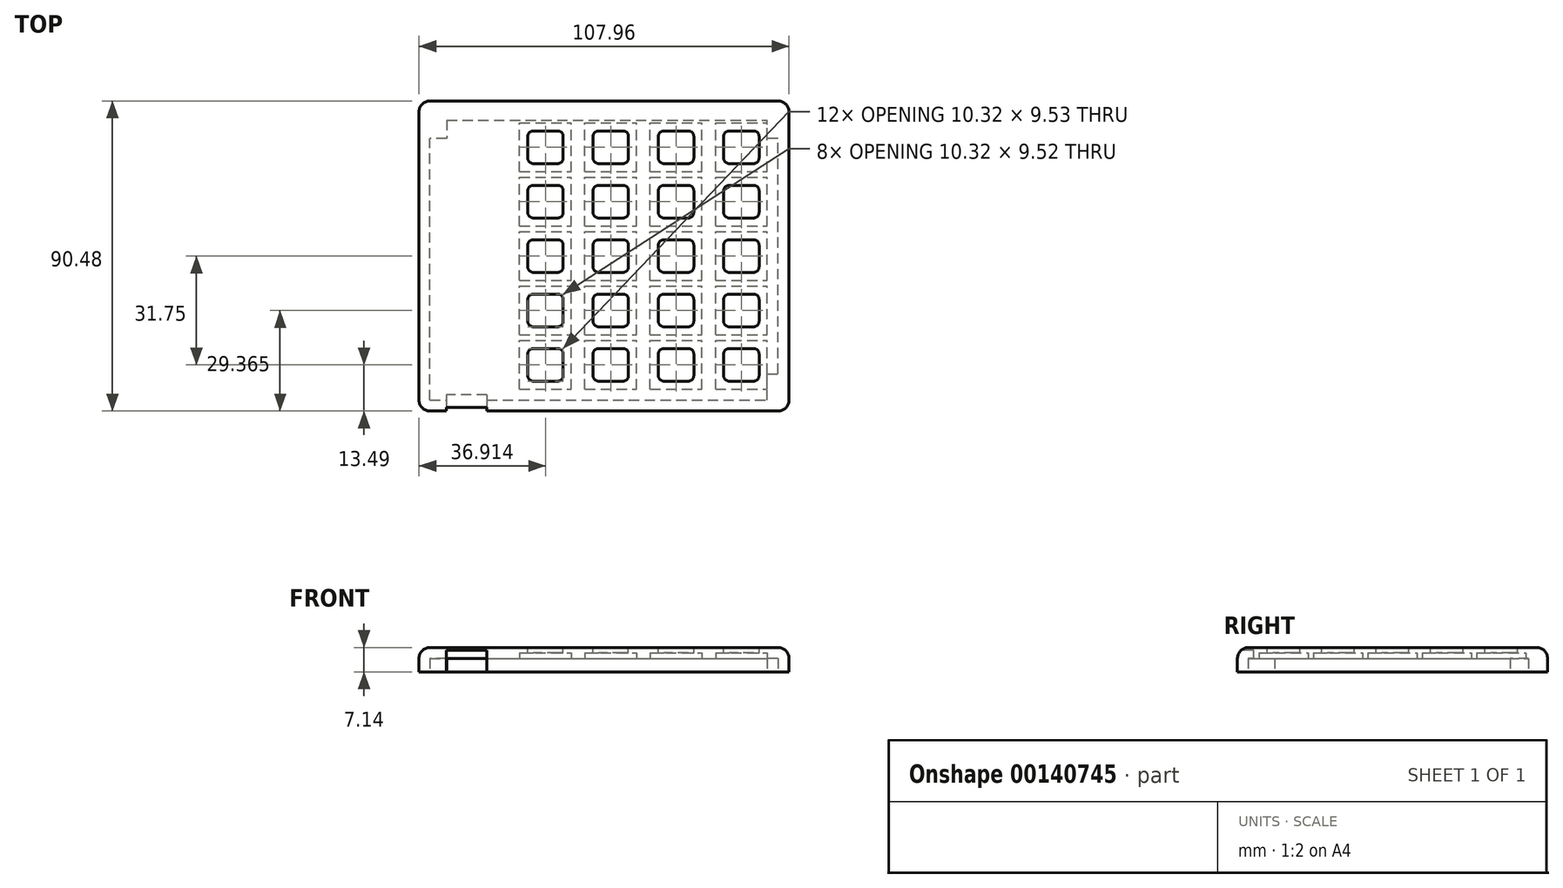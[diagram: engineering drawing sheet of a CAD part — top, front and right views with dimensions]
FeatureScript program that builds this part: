
annotation { "Feature Type Name" : "Feature", "Feature Type Description" : "" }
export const myFeature = defineFeature(function(context is Context, id is Id, definition is map)
    precondition{}
    {
        {
            var Q0;
            Q0=qCreatedBy(makeId("Top.planeOp"),FACE);
            var sketch = newSketch(context, id + "F0", { "sketchPlane" : qUnion([Q0])});
            skLineSegment(sketch, "E0.bottom", {"start": v(53.98, -45.24) * mm, "end": v(-53.98, -45.24) * mm});
            skLineSegment(sketch, "E0.top", {"start": v(53.98, 45.24) * mm, "end": v(-53.98, 45.24) * mm});
            skLineSegment(sketch, "E0.left", {"start": v(53.98, -45.24) * mm, "end": v(53.98, 45.24) * mm});
            skLineSegment(sketch, "E0.right", {"start": v(-53.98, -45.24) * mm, "end": v(-53.97, 45.24) * mm});
            skPoint(sketch, "E0.middle", {"position": v(0, 0) * mm});
            skSolve(sketch);
        }
        {
            var Q0;
            Q0=makeQuery(id+"F0.imprint","IMPRINT",FACE,{"disambiguationData":[TD([[makeQuery(id+"F0.imprint","IMPRINT",EDGE,{"derivedFrom":sQuery(id+"F0.wireOp",EDGE,"E0.bottom")}),-1.0]])]});
            extrude(context, id + "F1", {"entities" : qUnion([Q0]), "depth" : 7.14 * mm});
        }
        {
            var Q0;
            Q0=makeQuery(id+"F1.opExtrude","CAP_FACE",FACE,{"disambiguationData":[OSD([sQuery(id+"F0.wireOp",EDGE,"E0.bottom"),sQuery(id+"F0.wireOp",EDGE,"E0.top"),sQuery(id+"F0.wireOp",EDGE,"E0.left"),sQuery(id+"F0.wireOp",EDGE,"E0.right")])],"isStart":true});
            var sketch = newSketch(context, id + "F2", { "sketchPlane" : qUnion([Q0])});
            skLineSegment(sketch, "E1.0.0", {"start": v(53.98, 45.24) * mm, "end": v(-53.98, 45.24) * mm});
            skLineSegment(sketch, "E1.0.1", {"start": v(-53.98, 45.24) * mm, "end": v(-53.97, -45.24) * mm});
            skLineSegment(sketch, "E1.0.2", {"start": v(-53.97, -45.24) * mm, "end": v(53.98, -45.24) * mm});
            skLineSegment(sketch, "E1.0.3", {"start": v(53.98, -45.24) * mm, "end": v(53.98, 45.24) * mm});
            skLineSegment(sketch, "E2.bottom", {"start": v(-50.8, 42.07) * mm, "end": v(50.8, 42.07) * mm});
            skLineSegment(sketch, "E2.top", {"start": v(-50.8, -39.69) * mm, "end": v(50.8, -39.69) * mm});
            skLineSegment(sketch, "E2.left", {"start": v(-50.8, 42.07) * mm, "end": v(-50.8, -39.69) * mm});
            skLineSegment(sketch, "E2.right", {"start": v(50.8, 42.07) * mm, "end": v(50.8, -39.69) * mm});
            skSolve(sketch);
        }
        {
            var Q0;
            Q0=makeQuery(id+"F2.imprint","IMPRINT",FACE,{"disambiguationData":[TD([[makeQuery(id+"F2.imprint","IMPRINT",EDGE,{"derivedFrom":sQuery(id+"F2.wireOp",EDGE,"E2.bottom")}),-1.0]])]});
            extrude(context, id + "F3", {"entities" : qUnion([Q0]), "operationType" : NewBodyOperationType.REMOVE, "oppositeDirection" : true, "depth" : 3.97 * mm});
        }
        {
            var Q0;
            Q0=makeQuery(id+"F3.boolean.opBoolean","COPY",FACE,{"derivedFrom":makeQuery(id+"F3.opExtrude","CAP_FACE",FACE,{"disambiguationData":[OSD([sQuery(id+"F2.wireOp",EDGE,"E2.bottom"),sQuery(id+"F2.wireOp",EDGE,"E2.top"),sQuery(id+"F2.wireOp",EDGE,"E2.left"),sQuery(id+"F2.wireOp",EDGE,"E2.right")])],"isStart":false})});
            var sketch = newSketch(context, id + "F4", { "sketchPlane" : qUnion([Q0])});
            skLineSegment(sketch, "E3.0.0", {"start": v(50.8, 42.07) * mm, "end": v(-50.8, 42.07) * mm});
            skLineSegment(sketch, "E3.0.1", {"start": v(-50.8, 42.07) * mm, "end": v(-50.8, -39.69) * mm});
            skLineSegment(sketch, "E3.0.2", {"start": v(-50.8, -39.69) * mm, "end": v(50.8, -39.69) * mm});
            skLineSegment(sketch, "E3.0.3", {"start": v(50.8, -39.69) * mm, "end": v(50.8, 42.07) * mm});
            skLineSegment(sketch, "E4.bottom", {"start": v(50.8, 42.07) * mm, "end": v(50, 42.07) * mm});
            skLineSegment(sketch, "E4.top", {"start": v(50.8, 41.28) * mm, "end": v(50, 41.28) * mm});
            skLineSegment(sketch, "E4.left", {"start": v(50.8, 42.07) * mm, "end": v(50.8, 41.28) * mm});
            skLineSegment(sketch, "E4.right", {"start": v(50, 42.07) * mm, "end": v(50, 41.28) * mm});
            skLineSegment(sketch, "E5.bottom", {"start": v(50, 41.28) * mm, "end": v(46.04, 41.28) * mm});
            skLineSegment(sketch, "E5.top", {"start": v(50, 37.3) * mm, "end": v(46.04, 37.3) * mm});
            skLineSegment(sketch, "E5.left", {"start": v(50, 41.28) * mm, "end": v(50, 37.3) * mm});
            skLineSegment(sketch, "E5.right", {"start": v(46.04, 41.28) * mm, "end": v(46.04, 37.3) * mm});
            skLineSegment(sketch, "E6.bottom", {"start": v(46.04, 37.3) * mm, "end": v(34.13, 37.3) * mm});
            skLineSegment(sketch, "E6.top", {"start": v(46.04, 26.2) * mm, "end": v(34.13, 26.2) * mm});
            skLineSegment(sketch, "E6.left", {"start": v(46.04, 37.3) * mm, "end": v(46.04, 26.2) * mm});
            skLineSegment(sketch, "E6.right", {"start": v(34.13, 37.3) * mm, "end": v(34.13, 26.2) * mm});
            skLineSegment(sketch, "E7", {"start": v(41.14, -39.69) * mm, "end": v(41.14, -37.3) * mm});
            skLineSegment(sketch, "E8", {"start": v(-50.8, 34.78) * mm, "end": v(-23.02, 34.78) * mm});
            skLineSegment(sketch, "E9.0.1.0", {"start": v(46.04, 10.32) * mm, "end": v(34.13, 10.32) * mm});
            skLineSegment(sketch, "E9.0.1.1", {"start": v(46.04, 21.43) * mm, "end": v(46.04, 10.32) * mm});
            skLineSegment(sketch, "E9.0.1.2", {"start": v(46.04, 21.43) * mm, "end": v(34.13, 21.43) * mm});
            skLineSegment(sketch, "E9.0.1.3", {"start": v(34.13, 21.43) * mm, "end": v(34.13, 10.32) * mm});
            skLineSegment(sketch, "E9.0.2.0", {"start": v(46.04, -5.56) * mm, "end": v(34.13, -5.56) * mm});
            skLineSegment(sketch, "E9.0.2.1", {"start": v(46.04, 5.56) * mm, "end": v(46.04, -5.56) * mm});
            skLineSegment(sketch, "E9.0.2.2", {"start": v(46.04, 5.56) * mm, "end": v(34.13, 5.56) * mm});
            skLineSegment(sketch, "E9.0.2.3", {"start": v(34.13, 5.56) * mm, "end": v(34.13, -5.56) * mm});
            skLineSegment(sketch, "E9.0.3.0", {"start": v(46.04, -21.43) * mm, "end": v(34.13, -21.43) * mm});
            skLineSegment(sketch, "E9.0.3.1", {"start": v(46.04, -10.32) * mm, "end": v(46.04, -21.43) * mm});
            skLineSegment(sketch, "E9.0.3.2", {"start": v(46.04, -10.32) * mm, "end": v(34.13, -10.32) * mm});
            skLineSegment(sketch, "E9.0.3.3", {"start": v(34.13, -10.32) * mm, "end": v(34.13, -21.43) * mm});
            skLineSegment(sketch, "E9.0.4.0", {"start": v(46.04, -37.3) * mm, "end": v(34.13, -37.3) * mm});
            skLineSegment(sketch, "E9.0.4.1", {"start": v(46.04, -26.2) * mm, "end": v(46.04, -37.3) * mm});
            skLineSegment(sketch, "E9.0.4.2", {"start": v(46.04, -26.2) * mm, "end": v(34.13, -26.2) * mm});
            skLineSegment(sketch, "E9.0.4.3", {"start": v(34.13, -26.2) * mm, "end": v(34.13, -37.3) * mm});
            skLineSegment(sketch, "E9.1.0.0", {"start": v(26.99, 26.2) * mm, "end": v(15.08, 26.2) * mm});
            skLineSegment(sketch, "E9.1.0.1", {"start": v(26.99, 37.3) * mm, "end": v(26.99, 26.2) * mm});
            skLineSegment(sketch, "E9.1.0.2", {"start": v(26.99, 37.3) * mm, "end": v(15.08, 37.3) * mm});
            skLineSegment(sketch, "E9.1.0.3", {"start": v(15.08, 37.3) * mm, "end": v(15.08, 26.2) * mm});
            skLineSegment(sketch, "E9.1.1.0", {"start": v(26.99, 10.32) * mm, "end": v(15.08, 10.32) * mm});
            skLineSegment(sketch, "E9.1.1.1", {"start": v(26.99, 21.43) * mm, "end": v(26.99, 10.32) * mm});
            skLineSegment(sketch, "E9.1.1.2", {"start": v(26.99, 21.43) * mm, "end": v(15.08, 21.43) * mm});
            skLineSegment(sketch, "E9.1.1.3", {"start": v(15.08, 21.43) * mm, "end": v(15.08, 10.32) * mm});
            skLineSegment(sketch, "E9.1.2.0", {"start": v(26.99, -5.56) * mm, "end": v(15.08, -5.56) * mm});
            skLineSegment(sketch, "E9.1.2.1", {"start": v(26.99, 5.56) * mm, "end": v(26.99, -5.56) * mm});
            skLineSegment(sketch, "E9.1.2.2", {"start": v(26.99, 5.56) * mm, "end": v(15.08, 5.56) * mm});
            skLineSegment(sketch, "E9.1.2.3", {"start": v(15.08, 5.56) * mm, "end": v(15.08, -5.56) * mm});
            skLineSegment(sketch, "E9.1.3.0", {"start": v(26.99, -21.43) * mm, "end": v(15.08, -21.43) * mm});
            skLineSegment(sketch, "E9.1.3.1", {"start": v(26.99, -10.32) * mm, "end": v(26.99, -21.43) * mm});
            skLineSegment(sketch, "E9.1.3.2", {"start": v(26.99, -10.32) * mm, "end": v(15.08, -10.32) * mm});
            skLineSegment(sketch, "E9.1.3.3", {"start": v(15.08, -10.32) * mm, "end": v(15.08, -21.43) * mm});
            skLineSegment(sketch, "E9.1.4.0", {"start": v(26.99, -37.3) * mm, "end": v(15.08, -37.3) * mm});
            skLineSegment(sketch, "E9.1.4.1", {"start": v(26.99, -26.2) * mm, "end": v(26.99, -37.3) * mm});
            skLineSegment(sketch, "E9.1.4.2", {"start": v(26.99, -26.2) * mm, "end": v(15.08, -26.2) * mm});
            skLineSegment(sketch, "E9.1.4.3", {"start": v(15.08, -26.2) * mm, "end": v(15.08, -37.3) * mm});
            skLineSegment(sketch, "E9.2.0.0", {"start": v(7.94, 26.2) * mm, "end": v(-3.97, 26.2) * mm});
            skLineSegment(sketch, "E9.2.0.1", {"start": v(7.94, 37.3) * mm, "end": v(7.94, 26.2) * mm});
            skLineSegment(sketch, "E9.2.0.2", {"start": v(7.94, 37.3) * mm, "end": v(-3.97, 37.3) * mm});
            skLineSegment(sketch, "E9.2.0.3", {"start": v(-3.97, 37.3) * mm, "end": v(-3.97, 26.2) * mm});
            skLineSegment(sketch, "E9.2.1.0", {"start": v(7.94, 10.32) * mm, "end": v(-3.97, 10.32) * mm});
            skLineSegment(sketch, "E9.2.1.1", {"start": v(7.94, 21.43) * mm, "end": v(7.94, 10.32) * mm});
            skLineSegment(sketch, "E9.2.1.2", {"start": v(7.94, 21.43) * mm, "end": v(-3.97, 21.43) * mm});
            skLineSegment(sketch, "E9.2.1.3", {"start": v(-3.97, 21.43) * mm, "end": v(-3.97, 10.32) * mm});
            skLineSegment(sketch, "E9.2.2.0", {"start": v(7.94, -5.56) * mm, "end": v(-3.97, -5.56) * mm});
            skLineSegment(sketch, "E9.2.2.1", {"start": v(7.94, 5.56) * mm, "end": v(7.94, -5.56) * mm});
            skLineSegment(sketch, "E9.2.2.2", {"start": v(7.94, 5.56) * mm, "end": v(-3.97, 5.56) * mm});
            skLineSegment(sketch, "E9.2.2.3", {"start": v(-3.97, 5.56) * mm, "end": v(-3.97, -5.56) * mm});
            skLineSegment(sketch, "E9.2.3.0", {"start": v(7.94, -21.43) * mm, "end": v(-3.97, -21.43) * mm});
            skLineSegment(sketch, "E9.2.3.1", {"start": v(7.94, -10.32) * mm, "end": v(7.94, -21.43) * mm});
            skLineSegment(sketch, "E9.2.3.2", {"start": v(7.94, -10.32) * mm, "end": v(-3.97, -10.32) * mm});
            skLineSegment(sketch, "E9.2.3.3", {"start": v(-3.97, -10.32) * mm, "end": v(-3.97, -21.43) * mm});
            skLineSegment(sketch, "E9.2.4.0", {"start": v(7.94, -37.3) * mm, "end": v(-3.97, -37.3) * mm});
            skLineSegment(sketch, "E9.2.4.1", {"start": v(7.94, -26.2) * mm, "end": v(7.94, -37.3) * mm});
            skLineSegment(sketch, "E9.2.4.2", {"start": v(7.94, -26.2) * mm, "end": v(-3.97, -26.2) * mm});
            skLineSegment(sketch, "E9.2.4.3", {"start": v(-3.97, -26.2) * mm, "end": v(-3.97, -37.3) * mm});
            skLineSegment(sketch, "E9.3.0.0", {"start": v(-11.11, 26.2) * mm, "end": v(-23.02, 26.2) * mm});
            skLineSegment(sketch, "E9.3.0.1", {"start": v(-11.11, 37.3) * mm, "end": v(-11.11, 26.2) * mm});
            skLineSegment(sketch, "E9.3.0.2", {"start": v(-11.11, 37.3) * mm, "end": v(-23.02, 37.3) * mm});
            skLineSegment(sketch, "E9.3.0.3", {"start": v(-23.02, 37.3) * mm, "end": v(-23.02, 26.2) * mm});
            skLineSegment(sketch, "E9.3.1.0", {"start": v(-11.11, 10.32) * mm, "end": v(-23.02, 10.32) * mm});
            skLineSegment(sketch, "E9.3.1.1", {"start": v(-11.11, 21.43) * mm, "end": v(-11.11, 10.32) * mm});
            skLineSegment(sketch, "E9.3.1.2", {"start": v(-11.11, 21.43) * mm, "end": v(-23.02, 21.43) * mm});
            skLineSegment(sketch, "E9.3.1.3", {"start": v(-23.02, 21.43) * mm, "end": v(-23.02, 10.32) * mm});
            skLineSegment(sketch, "E9.3.2.0", {"start": v(-11.11, -5.56) * mm, "end": v(-23.02, -5.56) * mm});
            skLineSegment(sketch, "E9.3.2.1", {"start": v(-11.11, 5.56) * mm, "end": v(-11.11, -5.56) * mm});
            skLineSegment(sketch, "E9.3.2.2", {"start": v(-11.11, 5.56) * mm, "end": v(-23.02, 5.56) * mm});
            skLineSegment(sketch, "E9.3.2.3", {"start": v(-23.02, 5.56) * mm, "end": v(-23.02, -5.56) * mm});
            skLineSegment(sketch, "E9.3.3.0", {"start": v(-11.11, -21.43) * mm, "end": v(-23.02, -21.43) * mm});
            skLineSegment(sketch, "E9.3.3.1", {"start": v(-11.11, -10.32) * mm, "end": v(-11.11, -21.43) * mm});
            skLineSegment(sketch, "E9.3.3.2", {"start": v(-11.11, -10.32) * mm, "end": v(-23.02, -10.32) * mm});
            skLineSegment(sketch, "E9.3.3.3", {"start": v(-23.02, -10.32) * mm, "end": v(-23.02, -21.43) * mm});
            skLineSegment(sketch, "E9.3.4.0", {"start": v(-11.11, -37.3) * mm, "end": v(-23.02, -37.3) * mm});
            skLineSegment(sketch, "E9.3.4.1", {"start": v(-11.11, -26.2) * mm, "end": v(-11.11, -37.3) * mm});
            skLineSegment(sketch, "E9.3.4.2", {"start": v(-11.11, -26.2) * mm, "end": v(-23.02, -26.2) * mm});
            skLineSegment(sketch, "E9.3.4.3", {"start": v(-23.02, -26.2) * mm, "end": v(-23.02, -37.3) * mm});
            skLineSegment(sketch, "E9.direction1", {"start": v(34.13, 26.2) * mm, "end": v(15.08, 26.2) * mm, "construction": true});
            skLineSegment(sketch, "E9.direction2", {"start": v(34.13, 26.2) * mm, "end": v(34.13, 10.32) * mm, "construction": true});
            skLineSegment(sketch, "E10.bottom", {"start": v(32.54, 38.9) * mm, "end": v(47.62, 38.9) * mm});
            skLineSegment(sketch, "E10.top", {"start": v(32.54, 24.6) * mm, "end": v(47.62, 24.6) * mm});
            skLineSegment(sketch, "E10.left", {"start": v(32.54, 38.9) * mm, "end": v(32.54, 24.6) * mm});
            skLineSegment(sketch, "E10.right", {"start": v(47.62, 38.9) * mm, "end": v(47.62, 24.6) * mm});
            skLineSegment(sketch, "E11.0.1.0", {"start": v(32.54, 8.73) * mm, "end": v(47.62, 8.73) * mm});
            skLineSegment(sketch, "E11.0.1.1", {"start": v(32.54, 23.02) * mm, "end": v(32.54, 8.73) * mm});
            skLineSegment(sketch, "E11.0.1.2", {"start": v(32.54, 23.02) * mm, "end": v(47.62, 23.02) * mm});
            skLineSegment(sketch, "E11.0.1.3", {"start": v(47.62, 23.02) * mm, "end": v(47.62, 8.73) * mm});
            skLineSegment(sketch, "E11.0.2.0", {"start": v(32.54, -7.14) * mm, "end": v(47.62, -7.14) * mm});
            skLineSegment(sketch, "E11.0.2.1", {"start": v(32.54, 7.14) * mm, "end": v(32.54, -7.14) * mm});
            skLineSegment(sketch, "E11.0.2.2", {"start": v(32.54, 7.14) * mm, "end": v(47.62, 7.14) * mm});
            skLineSegment(sketch, "E11.0.2.3", {"start": v(47.62, 7.14) * mm, "end": v(47.62, -7.14) * mm});
            skLineSegment(sketch, "E11.0.3.0", {"start": v(32.54, -23.02) * mm, "end": v(47.62, -23.02) * mm});
            skLineSegment(sketch, "E11.0.3.1", {"start": v(32.54, -8.73) * mm, "end": v(32.54, -23.02) * mm});
            skLineSegment(sketch, "E11.0.3.2", {"start": v(32.54, -8.73) * mm, "end": v(47.62, -8.73) * mm});
            skLineSegment(sketch, "E11.0.3.3", {"start": v(47.62, -8.73) * mm, "end": v(47.62, -23.02) * mm});
            skLineSegment(sketch, "E11.0.4.0", {"start": v(32.54, -38.9) * mm, "end": v(47.62, -38.9) * mm});
            skLineSegment(sketch, "E11.0.4.1", {"start": v(32.54, -24.6) * mm, "end": v(32.54, -38.9) * mm});
            skLineSegment(sketch, "E11.0.4.2", {"start": v(32.54, -24.6) * mm, "end": v(47.62, -24.6) * mm});
            skLineSegment(sketch, "E11.0.4.3", {"start": v(47.62, -24.6) * mm, "end": v(47.62, -38.9) * mm});
            skLineSegment(sketch, "E11.1.0.0", {"start": v(13.5, 24.6) * mm, "end": v(28.57, 24.6) * mm});
            skLineSegment(sketch, "E11.1.0.1", {"start": v(13.5, 38.9) * mm, "end": v(13.5, 24.6) * mm});
            skLineSegment(sketch, "E11.1.0.2", {"start": v(13.5, 38.9) * mm, "end": v(28.57, 38.9) * mm});
            skLineSegment(sketch, "E11.1.0.3", {"start": v(28.57, 38.9) * mm, "end": v(28.57, 24.6) * mm});
            skLineSegment(sketch, "E11.1.1.0", {"start": v(13.5, 8.73) * mm, "end": v(28.57, 8.73) * mm});
            skLineSegment(sketch, "E11.1.1.1", {"start": v(13.5, 23.02) * mm, "end": v(13.5, 8.73) * mm});
            skLineSegment(sketch, "E11.1.1.2", {"start": v(13.5, 23.02) * mm, "end": v(28.57, 23.02) * mm});
            skLineSegment(sketch, "E11.1.1.3", {"start": v(28.57, 23.02) * mm, "end": v(28.57, 8.73) * mm});
            skLineSegment(sketch, "E11.1.2.0", {"start": v(13.5, -7.14) * mm, "end": v(28.57, -7.14) * mm});
            skLineSegment(sketch, "E11.1.2.1", {"start": v(13.5, 7.14) * mm, "end": v(13.5, -7.14) * mm});
            skLineSegment(sketch, "E11.1.2.2", {"start": v(13.5, 7.14) * mm, "end": v(28.57, 7.14) * mm});
            skLineSegment(sketch, "E11.1.2.3", {"start": v(28.57, 7.14) * mm, "end": v(28.57, -7.14) * mm});
            skLineSegment(sketch, "E11.1.3.0", {"start": v(13.5, -23.02) * mm, "end": v(28.57, -23.02) * mm});
            skLineSegment(sketch, "E11.1.3.1", {"start": v(13.5, -8.73) * mm, "end": v(13.5, -23.02) * mm});
            skLineSegment(sketch, "E11.1.3.2", {"start": v(13.5, -8.73) * mm, "end": v(28.57, -8.73) * mm});
            skLineSegment(sketch, "E11.1.3.3", {"start": v(28.57, -8.73) * mm, "end": v(28.57, -23.02) * mm});
            skLineSegment(sketch, "E11.1.4.0", {"start": v(13.5, -38.9) * mm, "end": v(28.57, -38.9) * mm});
            skLineSegment(sketch, "E11.1.4.1", {"start": v(13.5, -24.6) * mm, "end": v(13.5, -38.9) * mm});
            skLineSegment(sketch, "E11.1.4.2", {"start": v(13.5, -24.6) * mm, "end": v(28.57, -24.6) * mm});
            skLineSegment(sketch, "E11.1.4.3", {"start": v(28.57, -24.6) * mm, "end": v(28.57, -38.9) * mm});
            skLineSegment(sketch, "E11.2.0.0", {"start": v(-5.56, 24.6) * mm, "end": v(9.52, 24.6) * mm});
            skLineSegment(sketch, "E11.2.0.1", {"start": v(-5.56, 38.9) * mm, "end": v(-5.56, 24.6) * mm});
            skLineSegment(sketch, "E11.2.0.2", {"start": v(-5.56, 38.9) * mm, "end": v(9.52, 38.9) * mm});
            skLineSegment(sketch, "E11.2.0.3", {"start": v(9.52, 38.9) * mm, "end": v(9.52, 24.6) * mm});
            skLineSegment(sketch, "E11.2.1.0", {"start": v(-5.56, 8.73) * mm, "end": v(9.52, 8.73) * mm});
            skLineSegment(sketch, "E11.2.1.1", {"start": v(-5.56, 23.02) * mm, "end": v(-5.56, 8.73) * mm});
            skLineSegment(sketch, "E11.2.1.2", {"start": v(-5.56, 23.02) * mm, "end": v(9.52, 23.02) * mm});
            skLineSegment(sketch, "E11.2.1.3", {"start": v(9.52, 23.02) * mm, "end": v(9.52, 8.73) * mm});
            skLineSegment(sketch, "E11.2.2.0", {"start": v(-5.56, -7.14) * mm, "end": v(9.52, -7.14) * mm});
            skLineSegment(sketch, "E11.2.2.1", {"start": v(-5.56, 7.14) * mm, "end": v(-5.56, -7.14) * mm});
            skLineSegment(sketch, "E11.2.2.2", {"start": v(-5.56, 7.14) * mm, "end": v(9.52, 7.14) * mm});
            skLineSegment(sketch, "E11.2.2.3", {"start": v(9.52, 7.14) * mm, "end": v(9.52, -7.14) * mm});
            skLineSegment(sketch, "E11.2.3.0", {"start": v(-5.56, -23.02) * mm, "end": v(9.52, -23.02) * mm});
            skLineSegment(sketch, "E11.2.3.1", {"start": v(-5.56, -8.73) * mm, "end": v(-5.56, -23.02) * mm});
            skLineSegment(sketch, "E11.2.3.2", {"start": v(-5.56, -8.73) * mm, "end": v(9.52, -8.73) * mm});
            skLineSegment(sketch, "E11.2.3.3", {"start": v(9.52, -8.73) * mm, "end": v(9.52, -23.02) * mm});
            skLineSegment(sketch, "E11.2.4.0", {"start": v(-5.56, -38.9) * mm, "end": v(9.52, -38.9) * mm});
            skLineSegment(sketch, "E11.2.4.1", {"start": v(-5.56, -24.6) * mm, "end": v(-5.56, -38.9) * mm});
            skLineSegment(sketch, "E11.2.4.2", {"start": v(-5.56, -24.6) * mm, "end": v(9.52, -24.6) * mm});
            skLineSegment(sketch, "E11.2.4.3", {"start": v(9.52, -24.6) * mm, "end": v(9.52, -38.9) * mm});
            skLineSegment(sketch, "E11.3.0.0", {"start": v(-24.6, 24.6) * mm, "end": v(-9.53, 24.6) * mm});
            skLineSegment(sketch, "E11.3.0.1", {"start": v(-24.6, 38.9) * mm, "end": v(-24.6, 24.6) * mm});
            skLineSegment(sketch, "E11.3.0.2", {"start": v(-24.6, 38.9) * mm, "end": v(-9.53, 38.9) * mm});
            skLineSegment(sketch, "E11.3.0.3", {"start": v(-9.53, 38.9) * mm, "end": v(-9.53, 24.6) * mm});
            skLineSegment(sketch, "E11.3.1.0", {"start": v(-24.6, 8.73) * mm, "end": v(-9.53, 8.73) * mm});
            skLineSegment(sketch, "E11.3.1.1", {"start": v(-24.6, 23.02) * mm, "end": v(-24.6, 8.73) * mm});
            skLineSegment(sketch, "E11.3.1.2", {"start": v(-24.6, 23.02) * mm, "end": v(-9.53, 23.02) * mm});
            skLineSegment(sketch, "E11.3.1.3", {"start": v(-9.53, 23.02) * mm, "end": v(-9.53, 8.73) * mm});
            skLineSegment(sketch, "E11.3.2.0", {"start": v(-24.6, -7.14) * mm, "end": v(-9.53, -7.14) * mm});
            skLineSegment(sketch, "E11.3.2.1", {"start": v(-24.6, 7.14) * mm, "end": v(-24.6, -7.14) * mm});
            skLineSegment(sketch, "E11.3.2.2", {"start": v(-24.6, 7.14) * mm, "end": v(-9.53, 7.14) * mm});
            skLineSegment(sketch, "E11.3.2.3", {"start": v(-9.53, 7.14) * mm, "end": v(-9.53, -7.14) * mm});
            skLineSegment(sketch, "E11.3.3.0", {"start": v(-24.6, -23.02) * mm, "end": v(-9.53, -23.02) * mm});
            skLineSegment(sketch, "E11.3.3.1", {"start": v(-24.6, -8.73) * mm, "end": v(-24.6, -23.02) * mm});
            skLineSegment(sketch, "E11.3.3.2", {"start": v(-24.6, -8.73) * mm, "end": v(-9.53, -8.73) * mm});
            skLineSegment(sketch, "E11.3.3.3", {"start": v(-9.53, -8.73) * mm, "end": v(-9.53, -23.02) * mm});
            skLineSegment(sketch, "E11.3.4.0", {"start": v(-24.6, -38.9) * mm, "end": v(-9.53, -38.9) * mm});
            skLineSegment(sketch, "E11.3.4.1", {"start": v(-24.6, -24.6) * mm, "end": v(-24.6, -38.9) * mm});
            skLineSegment(sketch, "E11.3.4.2", {"start": v(-24.6, -24.6) * mm, "end": v(-9.53, -24.6) * mm});
            skLineSegment(sketch, "E11.3.4.3", {"start": v(-9.53, -24.6) * mm, "end": v(-9.53, -38.9) * mm});
            skLineSegment(sketch, "E11.direction1", {"start": v(32.54, 24.6) * mm, "end": v(13.5, 24.6) * mm, "construction": true});
            skLineSegment(sketch, "E11.direction2", {"start": v(32.54, 24.6) * mm, "end": v(32.54, 8.73) * mm, "construction": true});
            skSolve(sketch);
        }
        {
            var Q0;
            {var subQ3=sQuery(id+"F4.wireOp",EDGE,"E9.3.0.0");Q0=makeQuery(id+"F4.imprint","IMPRINT",FACE,{"disambiguationData":[TD([[makeQuery(id+"F4.imprint","IMPRINT",EDGE,{"derivedFrom":subQ3}),1.0]])]});}
            var Q1;
            {var subQ3=sQuery(id+"F4.wireOp",EDGE,"E9.3.0.0");Q1=makeQuery(id+"F4.imprint","IMPRINT",FACE,{"disambiguationData":[TD([[makeQuery(id+"F4.imprint","IMPRINT",EDGE,{"derivedFrom":subQ3}),-1.0]])]});}
            var Q2;
            Q2=makeQuery(id+"F4.imprint","IMPRINT",FACE,{"disambiguationData":[TD([[makeQuery(id+"F4.imprint","IMPRINT",EDGE,{"derivedFrom":sQuery(id+"F4.wireOp",EDGE,"E9.2.0.0")}),1.0]])]});
            var Q3;
            Q3=makeQuery(id+"F4.imprint","IMPRINT",FACE,{"disambiguationData":[TD([[makeQuery(id+"F4.imprint","IMPRINT",EDGE,{"derivedFrom":sQuery(id+"F4.wireOp",EDGE,"E9.2.0.0")}),-1.0]])]});
            var Q4;
            Q4=makeQuery(id+"F4.imprint","IMPRINT",FACE,{"disambiguationData":[TD([[makeQuery(id+"F4.imprint","IMPRINT",EDGE,{"derivedFrom":sQuery(id+"F4.wireOp",EDGE,"E9.1.0.0")}),1.0]])]});
            var Q5;
            Q5=makeQuery(id+"F4.imprint","IMPRINT",FACE,{"disambiguationData":[TD([[makeQuery(id+"F4.imprint","IMPRINT",EDGE,{"derivedFrom":sQuery(id+"F4.wireOp",EDGE,"E9.1.0.0")}),-1.0]])]});
            var Q6;
            {var subQ1=sQuery(id+"F4.wireOp",EDGE,"E6.bottom");Q6=makeQuery(id+"F4.imprint","IMPRINT",FACE,{"disambiguationData":[TD([[makeQuery(id+"F4.imprint","IMPRINT",EDGE,{"derivedFrom":subQ1}),-1.0]])]});}
            var Q7;
            Q7=makeQuery(id+"F4.imprint","IMPRINT",FACE,{"disambiguationData":[TD([[makeQuery(id+"F4.imprint","IMPRINT",EDGE,{"derivedFrom":sQuery(id+"F4.wireOp",EDGE,"E6.bottom")}),1.0]])]});
            var Q8;
            Q8=makeQuery(id+"F4.imprint","IMPRINT",FACE,{"disambiguationData":[TD([[makeQuery(id+"F4.imprint","IMPRINT",EDGE,{"derivedFrom":sQuery(id+"F4.wireOp",EDGE,"E9.0.1.0")}),1.0]])]});
            var Q9;
            Q9=makeQuery(id+"F4.imprint","IMPRINT",FACE,{"disambiguationData":[TD([[makeQuery(id+"F4.imprint","IMPRINT",EDGE,{"derivedFrom":sQuery(id+"F4.wireOp",EDGE,"E9.0.1.0")}),-1.0]])]});
            var Q10;
            Q10=makeQuery(id+"F4.imprint","IMPRINT",FACE,{"disambiguationData":[TD([[makeQuery(id+"F4.imprint","IMPRINT",EDGE,{"derivedFrom":sQuery(id+"F4.wireOp",EDGE,"E9.1.1.0")}),1.0]])]});
            var Q11;
            Q11=makeQuery(id+"F4.imprint","IMPRINT",FACE,{"disambiguationData":[TD([[makeQuery(id+"F4.imprint","IMPRINT",EDGE,{"derivedFrom":sQuery(id+"F4.wireOp",EDGE,"E9.1.1.0")}),-1.0]])]});
            var Q12;
            Q12=makeQuery(id+"F4.imprint","IMPRINT",FACE,{"disambiguationData":[TD([[makeQuery(id+"F4.imprint","IMPRINT",EDGE,{"derivedFrom":sQuery(id+"F4.wireOp",EDGE,"E9.2.1.0")}),1.0]])]});
            var Q13;
            Q13=makeQuery(id+"F4.imprint","IMPRINT",FACE,{"disambiguationData":[TD([[makeQuery(id+"F4.imprint","IMPRINT",EDGE,{"derivedFrom":sQuery(id+"F4.wireOp",EDGE,"E9.2.1.0")}),-1.0]])]});
            var Q14;
            Q14=makeQuery(id+"F4.imprint","IMPRINT",FACE,{"disambiguationData":[TD([[makeQuery(id+"F4.imprint","IMPRINT",EDGE,{"derivedFrom":sQuery(id+"F4.wireOp",EDGE,"E9.3.1.0")}),1.0]])]});
            var Q15;
            Q15=makeQuery(id+"F4.imprint","IMPRINT",FACE,{"disambiguationData":[TD([[makeQuery(id+"F4.imprint","IMPRINT",EDGE,{"derivedFrom":sQuery(id+"F4.wireOp",EDGE,"E9.3.1.0")}),-1.0]])]});
            var Q16;
            Q16=makeQuery(id+"F4.imprint","IMPRINT",FACE,{"disambiguationData":[TD([[makeQuery(id+"F4.imprint","IMPRINT",EDGE,{"derivedFrom":sQuery(id+"F4.wireOp",EDGE,"E9.3.2.0")}),1.0]])]});
            var Q17;
            Q17=makeQuery(id+"F4.imprint","IMPRINT",FACE,{"disambiguationData":[TD([[makeQuery(id+"F4.imprint","IMPRINT",EDGE,{"derivedFrom":sQuery(id+"F4.wireOp",EDGE,"E9.3.2.0")}),-1.0]])]});
            var Q18;
            Q18=makeQuery(id+"F4.imprint","IMPRINT",FACE,{"disambiguationData":[TD([[makeQuery(id+"F4.imprint","IMPRINT",EDGE,{"derivedFrom":sQuery(id+"F4.wireOp",EDGE,"E9.2.2.0")}),1.0]])]});
            var Q19;
            Q19=makeQuery(id+"F4.imprint","IMPRINT",FACE,{"disambiguationData":[TD([[makeQuery(id+"F4.imprint","IMPRINT",EDGE,{"derivedFrom":sQuery(id+"F4.wireOp",EDGE,"E9.2.2.0")}),-1.0]])]});
            var Q20;
            Q20=makeQuery(id+"F4.imprint","IMPRINT",FACE,{"disambiguationData":[TD([[makeQuery(id+"F4.imprint","IMPRINT",EDGE,{"derivedFrom":sQuery(id+"F4.wireOp",EDGE,"E9.1.2.0")}),1.0]])]});
            var Q21;
            Q21=makeQuery(id+"F4.imprint","IMPRINT",FACE,{"disambiguationData":[TD([[makeQuery(id+"F4.imprint","IMPRINT",EDGE,{"derivedFrom":sQuery(id+"F4.wireOp",EDGE,"E9.1.2.0")}),-1.0]])]});
            var Q22;
            Q22=makeQuery(id+"F4.imprint","IMPRINT",FACE,{"disambiguationData":[TD([[makeQuery(id+"F4.imprint","IMPRINT",EDGE,{"derivedFrom":sQuery(id+"F4.wireOp",EDGE,"E9.0.2.0")}),-1.0]])]});
            var Q23;
            Q23=makeQuery(id+"F4.imprint","IMPRINT",FACE,{"disambiguationData":[TD([[makeQuery(id+"F4.imprint","IMPRINT",EDGE,{"derivedFrom":sQuery(id+"F4.wireOp",EDGE,"E9.0.2.0")}),1.0]])]});
            var Q24;
            Q24=makeQuery(id+"F4.imprint","IMPRINT",FACE,{"disambiguationData":[TD([[makeQuery(id+"F4.imprint","IMPRINT",EDGE,{"derivedFrom":sQuery(id+"F4.wireOp",EDGE,"E9.3.3.0")}),1.0]])]});
            var Q25;
            Q25=makeQuery(id+"F4.imprint","IMPRINT",FACE,{"disambiguationData":[TD([[makeQuery(id+"F4.imprint","IMPRINT",EDGE,{"derivedFrom":sQuery(id+"F4.wireOp",EDGE,"E9.3.3.0")}),-1.0]])]});
            var Q26;
            Q26=makeQuery(id+"F4.imprint","IMPRINT",FACE,{"disambiguationData":[TD([[makeQuery(id+"F4.imprint","IMPRINT",EDGE,{"derivedFrom":sQuery(id+"F4.wireOp",EDGE,"E9.2.3.0")}),1.0]])]});
            var Q27;
            Q27=makeQuery(id+"F4.imprint","IMPRINT",FACE,{"disambiguationData":[TD([[makeQuery(id+"F4.imprint","IMPRINT",EDGE,{"derivedFrom":sQuery(id+"F4.wireOp",EDGE,"E9.2.3.0")}),-1.0]])]});
            var Q28;
            Q28=makeQuery(id+"F4.imprint","IMPRINT",FACE,{"disambiguationData":[TD([[makeQuery(id+"F4.imprint","IMPRINT",EDGE,{"derivedFrom":sQuery(id+"F4.wireOp",EDGE,"E9.1.3.0")}),1.0]])]});
            var Q29;
            Q29=makeQuery(id+"F4.imprint","IMPRINT",FACE,{"disambiguationData":[TD([[makeQuery(id+"F4.imprint","IMPRINT",EDGE,{"derivedFrom":sQuery(id+"F4.wireOp",EDGE,"E9.1.3.0")}),-1.0]])]});
            var Q30;
            Q30=makeQuery(id+"F4.imprint","IMPRINT",FACE,{"disambiguationData":[TD([[makeQuery(id+"F4.imprint","IMPRINT",EDGE,{"derivedFrom":sQuery(id+"F4.wireOp",EDGE,"E9.0.3.0")}),1.0]])]});
            var Q31;
            Q31=makeQuery(id+"F4.imprint","IMPRINT",FACE,{"disambiguationData":[TD([[makeQuery(id+"F4.imprint","IMPRINT",EDGE,{"derivedFrom":sQuery(id+"F4.wireOp",EDGE,"E9.0.3.0")}),-1.0]])]});
            var Q32;
            {var subQ3=sQuery(id+"F4.wireOp",EDGE,"E9.0.4.1");Q32=makeQuery(id+"F4.imprint","IMPRINT",FACE,{"disambiguationData":[TD([[makeQuery(id+"F4.imprint","IMPRINT",EDGE,{"derivedFrom":subQ3}),1.0]])]});}
            var Q33;
            {var subQ0=sQuery(id+"F4.wireOp",EDGE,"E9.0.4.1");Q33=makeQuery(id+"F4.imprint","IMPRINT",FACE,{"disambiguationData":[TD([[makeQuery(id+"F4.imprint","IMPRINT",EDGE,{"derivedFrom":subQ0}),-1.0]])]});}
            var Q34;
            Q34=makeQuery(id+"F4.imprint","IMPRINT",FACE,{"disambiguationData":[TD([[makeQuery(id+"F4.imprint","IMPRINT",EDGE,{"derivedFrom":sQuery(id+"F4.wireOp",EDGE,"E9.1.4.0")}),1.0]])]});
            var Q35;
            Q35=makeQuery(id+"F4.imprint","IMPRINT",FACE,{"disambiguationData":[TD([[makeQuery(id+"F4.imprint","IMPRINT",EDGE,{"derivedFrom":sQuery(id+"F4.wireOp",EDGE,"E9.1.4.0")}),-1.0]])]});
            var Q36;
            Q36=makeQuery(id+"F4.imprint","IMPRINT",FACE,{"disambiguationData":[TD([[makeQuery(id+"F4.imprint","IMPRINT",EDGE,{"derivedFrom":sQuery(id+"F4.wireOp",EDGE,"E9.2.4.0")}),1.0]])]});
            var Q37;
            Q37=makeQuery(id+"F4.imprint","IMPRINT",FACE,{"disambiguationData":[TD([[makeQuery(id+"F4.imprint","IMPRINT",EDGE,{"derivedFrom":sQuery(id+"F4.wireOp",EDGE,"E9.2.4.0")}),-1.0]])]});
            var Q38;
            Q38=makeQuery(id+"F4.imprint","IMPRINT",FACE,{"disambiguationData":[TD([[makeQuery(id+"F4.imprint","IMPRINT",EDGE,{"derivedFrom":sQuery(id+"F4.wireOp",EDGE,"E9.3.4.0")}),-1.0]])]});
            var Q39;
            Q39=makeQuery(id+"F4.imprint","IMPRINT",FACE,{"disambiguationData":[TD([[makeQuery(id+"F4.imprint","IMPRINT",EDGE,{"derivedFrom":sQuery(id+"F4.wireOp",EDGE,"E9.3.4.0")}),1.0]])]});
            var Q40;
            {var subQ3=sQuery(id+"F4.wireOp",EDGE,"E10.right");var subQ5=sQuery(id+"F4.wireOp",EDGE,"E10.bottom");var subQ7=makeQuery(id+"F4.imprint","INTERSECT",VERTEX,{"derivedFrom":[subQ5,subQ3]});Q40=makeQuery(id+"F4.imprint","IMPRINT",FACE,{"disambiguationData":[TD([[makeQuery(id+"F4.imprint","IMPRINT",EDGE,{"disambiguationData":[TD([[subQ7,1.0]])],"derivedFrom":subQ5}),-1.0]])]});}
            extrude(context, id + "F5", {"entities" : qUnion([Q0, Q1, Q2, Q3, Q4, Q5, Q6, Q7, Q8, Q9, Q10, Q11, Q12, Q13, Q14, Q15, Q16, Q17, Q18, Q19, Q20, Q21, Q22, Q23, Q24, Q25, Q26, Q27, Q28, Q29, Q30, Q31, Q32, Q33, Q34, Q35, Q36, Q37, Q38, Q39, Q40]), "operationType" : NewBodyOperationType.REMOVE, "oppositeDirection" : true, "depth" : 1.59 * mm});
        }
        {
            var Q0;
            Q0=makeQuery(id+"F5.boolean.opBoolean","COPY",FACE,{"derivedFrom":makeQuery(id+"F5.opExtrude","CAP_FACE",FACE,{"disambiguationData":[OSD([sQuery(id+"F4.wireOp",EDGE,"E11.1.0.0"),sQuery(id+"F4.wireOp",EDGE,"E11.1.0.1"),sQuery(id+"F4.wireOp",EDGE,"E11.1.0.2"),sQuery(id+"F4.wireOp",EDGE,"E11.1.0.3")])],"isStart":false})});
            var sketch = newSketch(context, id + "F6", { "sketchPlane" : qUnion([Q0])});
            skLineSegment(sketch, "E12.bottom", {"start": v(36.51, 36.51) * mm, "end": v(43.66, 36.51) * mm});
            skLineSegment(sketch, "E12.top", {"start": v(36.51, 26.99) * mm, "end": v(43.66, 26.99) * mm});
            skLineSegment(sketch, "E12.left", {"start": v(34.93, 34.93) * mm, "end": v(34.93, 28.58) * mm});
            skLineSegment(sketch, "E12.right", {"start": v(45.24, 34.93) * mm, "end": v(45.24, 28.58) * mm});
            skPoint(sketch, "E13.visualSharp", {"position": v(34.93, 36.51) * mm});
            skArc(sketch, "E13.filletArc", {"start": v(36.51, 36.51) * mm, "mid": v(35.39, 36.05) * mm, "end": v(34.93, 34.93) * mm});
            skPoint(sketch, "E14.visualSharp", {"position": v(45.24, 36.51) * mm});
            skArc(sketch, "E14.filletArc", {"start": v(45.24, 34.93) * mm, "mid": v(44.78, 36.05) * mm, "end": v(43.66, 36.51) * mm});
            skPoint(sketch, "E15.visualSharp", {"position": v(45.24, 26.99) * mm});
            skArc(sketch, "E15.filletArc", {"start": v(43.66, 26.99) * mm, "mid": v(44.78, 27.45) * mm, "end": v(45.24, 28.58) * mm});
            skPoint(sketch, "E16.visualSharp", {"position": v(34.93, 26.99) * mm});
            skArc(sketch, "E16.filletArc", {"start": v(34.93, 28.58) * mm, "mid": v(35.39, 27.45) * mm, "end": v(36.51, 26.99) * mm});
            skLineSegment(sketch, "E17.0.1.0", {"start": v(36.51, 11.11) * mm, "end": v(43.66, 11.11) * mm});
            skArc(sketch, "E17.0.1.1", {"start": v(34.93, 12.7) * mm, "mid": v(35.39, 11.58) * mm, "end": v(36.51, 11.11) * mm});
            skLineSegment(sketch, "E17.0.1.2", {"start": v(34.93, 19.05) * mm, "end": v(34.93, 12.7) * mm});
            skArc(sketch, "E17.0.1.3", {"start": v(36.51, 20.64) * mm, "mid": v(35.39, 20.17) * mm, "end": v(34.93, 19.05) * mm});
            skLineSegment(sketch, "E17.0.1.4", {"start": v(36.51, 20.64) * mm, "end": v(43.66, 20.64) * mm});
            skArc(sketch, "E17.0.1.5", {"start": v(45.24, 19.05) * mm, "mid": v(44.78, 20.17) * mm, "end": v(43.66, 20.64) * mm});
            skLineSegment(sketch, "E17.0.1.6", {"start": v(45.24, 19.05) * mm, "end": v(45.24, 12.7) * mm});
            skArc(sketch, "E17.0.1.7", {"start": v(43.66, 11.11) * mm, "mid": v(44.78, 11.58) * mm, "end": v(45.24, 12.7) * mm});
            skLineSegment(sketch, "E17.0.2.0", {"start": v(36.51, -4.76) * mm, "end": v(43.66, -4.76) * mm});
            skArc(sketch, "E17.0.2.1", {"start": v(34.93, -3.17) * mm, "mid": v(35.39, -4.3) * mm, "end": v(36.51, -4.76) * mm});
            skLineSegment(sketch, "E17.0.2.2", {"start": v(34.93, 3.18) * mm, "end": v(34.93, -3.17) * mm});
            skArc(sketch, "E17.0.2.3", {"start": v(36.51, 4.76) * mm, "mid": v(35.39, 4.3) * mm, "end": v(34.93, 3.18) * mm});
            skLineSegment(sketch, "E17.0.2.4", {"start": v(36.51, 4.76) * mm, "end": v(43.66, 4.76) * mm});
            skArc(sketch, "E17.0.2.5", {"start": v(45.24, 3.18) * mm, "mid": v(44.78, 4.3) * mm, "end": v(43.66, 4.76) * mm});
            skLineSegment(sketch, "E17.0.2.6", {"start": v(45.24, 3.18) * mm, "end": v(45.24, -3.17) * mm});
            skArc(sketch, "E17.0.2.7", {"start": v(43.66, -4.76) * mm, "mid": v(44.78, -4.3) * mm, "end": v(45.24, -3.17) * mm});
            skLineSegment(sketch, "E17.0.3.0", {"start": v(36.51, -20.64) * mm, "end": v(43.66, -20.64) * mm});
            skArc(sketch, "E17.0.3.1", {"start": v(34.93, -19.05) * mm, "mid": v(35.39, -20.17) * mm, "end": v(36.51, -20.64) * mm});
            skLineSegment(sketch, "E17.0.3.2", {"start": v(34.93, -12.7) * mm, "end": v(34.93, -19.05) * mm});
            skArc(sketch, "E17.0.3.3", {"start": v(36.51, -11.11) * mm, "mid": v(35.39, -11.58) * mm, "end": v(34.93, -12.7) * mm});
            skLineSegment(sketch, "E17.0.3.4", {"start": v(36.51, -11.11) * mm, "end": v(43.66, -11.11) * mm});
            skArc(sketch, "E17.0.3.5", {"start": v(45.24, -12.7) * mm, "mid": v(44.78, -11.58) * mm, "end": v(43.66, -11.11) * mm});
            skLineSegment(sketch, "E17.0.3.6", {"start": v(45.24, -12.7) * mm, "end": v(45.24, -19.05) * mm});
            skArc(sketch, "E17.0.3.7", {"start": v(43.66, -20.64) * mm, "mid": v(44.78, -20.17) * mm, "end": v(45.24, -19.05) * mm});
            skLineSegment(sketch, "E17.0.4.0", {"start": v(36.51, -36.51) * mm, "end": v(43.66, -36.51) * mm});
            skArc(sketch, "E17.0.4.1", {"start": v(34.93, -34.92) * mm, "mid": v(35.39, -36.05) * mm, "end": v(36.51, -36.51) * mm});
            skLineSegment(sketch, "E17.0.4.2", {"start": v(34.93, -28.57) * mm, "end": v(34.93, -34.92) * mm});
            skArc(sketch, "E17.0.4.3", {"start": v(36.51, -26.99) * mm, "mid": v(35.39, -27.45) * mm, "end": v(34.93, -28.57) * mm});
            skLineSegment(sketch, "E17.0.4.4", {"start": v(36.51, -26.99) * mm, "end": v(43.66, -26.99) * mm});
            skArc(sketch, "E17.0.4.5", {"start": v(45.24, -28.57) * mm, "mid": v(44.78, -27.45) * mm, "end": v(43.66, -26.99) * mm});
            skLineSegment(sketch, "E17.0.4.6", {"start": v(45.24, -28.57) * mm, "end": v(45.24, -34.92) * mm});
            skArc(sketch, "E17.0.4.7", {"start": v(43.66, -36.51) * mm, "mid": v(44.78, -36.05) * mm, "end": v(45.24, -34.92) * mm});
            skLineSegment(sketch, "E17.1.0.0", {"start": v(17.46, 26.99) * mm, "end": v(24.6, 26.99) * mm});
            skArc(sketch, "E17.1.0.1", {"start": v(15.88, 28.58) * mm, "mid": v(16.34, 27.45) * mm, "end": v(17.46, 26.99) * mm});
            skLineSegment(sketch, "E17.1.0.2", {"start": v(15.88, 34.93) * mm, "end": v(15.88, 28.58) * mm});
            skArc(sketch, "E17.1.0.3", {"start": v(17.46, 36.51) * mm, "mid": v(16.34, 36.05) * mm, "end": v(15.88, 34.93) * mm});
            skLineSegment(sketch, "E17.1.0.4", {"start": v(17.46, 36.51) * mm, "end": v(24.6, 36.51) * mm});
            skArc(sketch, "E17.1.0.5", {"start": v(26.2, 34.93) * mm, "mid": v(25.73, 36.05) * mm, "end": v(24.6, 36.51) * mm});
            skLineSegment(sketch, "E17.1.0.6", {"start": v(26.2, 34.93) * mm, "end": v(26.2, 28.58) * mm});
            skArc(sketch, "E17.1.0.7", {"start": v(24.6, 26.99) * mm, "mid": v(25.73, 27.45) * mm, "end": v(26.2, 28.58) * mm});
            skLineSegment(sketch, "E17.1.1.0", {"start": v(17.46, 11.11) * mm, "end": v(24.6, 11.11) * mm});
            skArc(sketch, "E17.1.1.1", {"start": v(15.88, 12.7) * mm, "mid": v(16.34, 11.58) * mm, "end": v(17.46, 11.11) * mm});
            skLineSegment(sketch, "E17.1.1.2", {"start": v(15.88, 19.05) * mm, "end": v(15.88, 12.7) * mm});
            skArc(sketch, "E17.1.1.3", {"start": v(17.46, 20.64) * mm, "mid": v(16.34, 20.17) * mm, "end": v(15.88, 19.05) * mm});
            skLineSegment(sketch, "E17.1.1.4", {"start": v(17.46, 20.64) * mm, "end": v(24.6, 20.64) * mm});
            skArc(sketch, "E17.1.1.5", {"start": v(26.2, 19.05) * mm, "mid": v(25.73, 20.17) * mm, "end": v(24.6, 20.64) * mm});
            skLineSegment(sketch, "E17.1.1.6", {"start": v(26.2, 19.05) * mm, "end": v(26.2, 12.7) * mm});
            skArc(sketch, "E17.1.1.7", {"start": v(24.6, 11.11) * mm, "mid": v(25.73, 11.58) * mm, "end": v(26.2, 12.7) * mm});
            skLineSegment(sketch, "E17.1.2.0", {"start": v(17.46, -4.76) * mm, "end": v(24.6, -4.76) * mm});
            skArc(sketch, "E17.1.2.1", {"start": v(15.88, -3.17) * mm, "mid": v(16.34, -4.3) * mm, "end": v(17.46, -4.76) * mm});
            skLineSegment(sketch, "E17.1.2.2", {"start": v(15.88, 3.18) * mm, "end": v(15.88, -3.17) * mm});
            skArc(sketch, "E17.1.2.3", {"start": v(17.46, 4.76) * mm, "mid": v(16.34, 4.3) * mm, "end": v(15.88, 3.18) * mm});
            skLineSegment(sketch, "E17.1.2.4", {"start": v(17.46, 4.76) * mm, "end": v(24.6, 4.76) * mm});
            skArc(sketch, "E17.1.2.5", {"start": v(26.2, 3.18) * mm, "mid": v(25.73, 4.3) * mm, "end": v(24.6, 4.76) * mm});
            skLineSegment(sketch, "E17.1.2.6", {"start": v(26.2, 3.18) * mm, "end": v(26.2, -3.17) * mm});
            skArc(sketch, "E17.1.2.7", {"start": v(24.6, -4.76) * mm, "mid": v(25.73, -4.3) * mm, "end": v(26.2, -3.17) * mm});
            skLineSegment(sketch, "E17.1.3.0", {"start": v(17.46, -20.64) * mm, "end": v(24.6, -20.64) * mm});
            skArc(sketch, "E17.1.3.1", {"start": v(15.88, -19.05) * mm, "mid": v(16.34, -20.17) * mm, "end": v(17.46, -20.64) * mm});
            skLineSegment(sketch, "E17.1.3.2", {"start": v(15.88, -12.7) * mm, "end": v(15.88, -19.05) * mm});
            skArc(sketch, "E17.1.3.3", {"start": v(17.46, -11.11) * mm, "mid": v(16.34, -11.58) * mm, "end": v(15.88, -12.7) * mm});
            skLineSegment(sketch, "E17.1.3.4", {"start": v(17.46, -11.11) * mm, "end": v(24.6, -11.11) * mm});
            skArc(sketch, "E17.1.3.5", {"start": v(26.2, -12.7) * mm, "mid": v(25.73, -11.58) * mm, "end": v(24.6, -11.11) * mm});
            skLineSegment(sketch, "E17.1.3.6", {"start": v(26.2, -12.7) * mm, "end": v(26.2, -19.05) * mm});
            skArc(sketch, "E17.1.3.7", {"start": v(24.6, -20.64) * mm, "mid": v(25.73, -20.17) * mm, "end": v(26.2, -19.05) * mm});
            skLineSegment(sketch, "E17.1.4.0", {"start": v(17.46, -36.51) * mm, "end": v(24.6, -36.51) * mm});
            skArc(sketch, "E17.1.4.1", {"start": v(15.88, -34.92) * mm, "mid": v(16.34, -36.05) * mm, "end": v(17.46, -36.51) * mm});
            skLineSegment(sketch, "E17.1.4.2", {"start": v(15.88, -28.57) * mm, "end": v(15.88, -34.92) * mm});
            skArc(sketch, "E17.1.4.3", {"start": v(17.46, -26.99) * mm, "mid": v(16.34, -27.45) * mm, "end": v(15.88, -28.57) * mm});
            skLineSegment(sketch, "E17.1.4.4", {"start": v(17.46, -26.99) * mm, "end": v(24.6, -26.99) * mm});
            skArc(sketch, "E17.1.4.5", {"start": v(26.2, -28.57) * mm, "mid": v(25.73, -27.45) * mm, "end": v(24.6, -26.99) * mm});
            skLineSegment(sketch, "E17.1.4.6", {"start": v(26.2, -28.57) * mm, "end": v(26.2, -34.92) * mm});
            skArc(sketch, "E17.1.4.7", {"start": v(24.6, -36.51) * mm, "mid": v(25.73, -36.05) * mm, "end": v(26.2, -34.92) * mm});
            skLineSegment(sketch, "E17.2.0.0", {"start": v(-1.59, 26.99) * mm, "end": v(5.56, 26.99) * mm});
            skArc(sketch, "E17.2.0.1", {"start": v(-3.17, 28.58) * mm, "mid": v(-2.71, 27.45) * mm, "end": v(-1.59, 26.99) * mm});
            skLineSegment(sketch, "E17.2.0.2", {"start": v(-3.17, 34.93) * mm, "end": v(-3.17, 28.58) * mm});
            skArc(sketch, "E17.2.0.3", {"start": v(-1.59, 36.51) * mm, "mid": v(-2.71, 36.05) * mm, "end": v(-3.17, 34.93) * mm});
            skLineSegment(sketch, "E17.2.0.4", {"start": v(-1.59, 36.51) * mm, "end": v(5.56, 36.51) * mm});
            skArc(sketch, "E17.2.0.5", {"start": v(7.14, 34.93) * mm, "mid": v(6.68, 36.05) * mm, "end": v(5.56, 36.51) * mm});
            skLineSegment(sketch, "E17.2.0.6", {"start": v(7.14, 34.93) * mm, "end": v(7.14, 28.58) * mm});
            skArc(sketch, "E17.2.0.7", {"start": v(5.56, 26.99) * mm, "mid": v(6.68, 27.45) * mm, "end": v(7.14, 28.58) * mm});
            skLineSegment(sketch, "E17.2.1.0", {"start": v(-1.59, 11.11) * mm, "end": v(5.56, 11.11) * mm});
            skArc(sketch, "E17.2.1.1", {"start": v(-3.17, 12.7) * mm, "mid": v(-2.71, 11.58) * mm, "end": v(-1.59, 11.11) * mm});
            skLineSegment(sketch, "E17.2.1.2", {"start": v(-3.17, 19.05) * mm, "end": v(-3.17, 12.7) * mm});
            skArc(sketch, "E17.2.1.3", {"start": v(-1.59, 20.64) * mm, "mid": v(-2.71, 20.17) * mm, "end": v(-3.17, 19.05) * mm});
            skLineSegment(sketch, "E17.2.1.4", {"start": v(-1.59, 20.64) * mm, "end": v(5.56, 20.64) * mm});
            skArc(sketch, "E17.2.1.5", {"start": v(7.14, 19.05) * mm, "mid": v(6.68, 20.17) * mm, "end": v(5.56, 20.64) * mm});
            skLineSegment(sketch, "E17.2.1.6", {"start": v(7.14, 19.05) * mm, "end": v(7.14, 12.7) * mm});
            skArc(sketch, "E17.2.1.7", {"start": v(5.56, 11.11) * mm, "mid": v(6.68, 11.58) * mm, "end": v(7.14, 12.7) * mm});
            skLineSegment(sketch, "E17.2.2.0", {"start": v(-1.59, -4.76) * mm, "end": v(5.56, -4.76) * mm});
            skArc(sketch, "E17.2.2.1", {"start": v(-3.17, -3.17) * mm, "mid": v(-2.71, -4.3) * mm, "end": v(-1.59, -4.76) * mm});
            skLineSegment(sketch, "E17.2.2.2", {"start": v(-3.17, 3.18) * mm, "end": v(-3.17, -3.17) * mm});
            skArc(sketch, "E17.2.2.3", {"start": v(-1.59, 4.76) * mm, "mid": v(-2.71, 4.3) * mm, "end": v(-3.17, 3.18) * mm});
            skLineSegment(sketch, "E17.2.2.4", {"start": v(-1.59, 4.76) * mm, "end": v(5.56, 4.76) * mm});
            skArc(sketch, "E17.2.2.5", {"start": v(7.14, 3.18) * mm, "mid": v(6.68, 4.3) * mm, "end": v(5.56, 4.76) * mm});
            skLineSegment(sketch, "E17.2.2.6", {"start": v(7.14, 3.18) * mm, "end": v(7.14, -3.17) * mm});
            skArc(sketch, "E17.2.2.7", {"start": v(5.56, -4.76) * mm, "mid": v(6.68, -4.3) * mm, "end": v(7.14, -3.17) * mm});
            skLineSegment(sketch, "E17.2.3.0", {"start": v(-1.59, -20.64) * mm, "end": v(5.56, -20.64) * mm});
            skArc(sketch, "E17.2.3.1", {"start": v(-3.17, -19.05) * mm, "mid": v(-2.71, -20.17) * mm, "end": v(-1.59, -20.64) * mm});
            skLineSegment(sketch, "E17.2.3.2", {"start": v(-3.17, -12.7) * mm, "end": v(-3.17, -19.05) * mm});
            skArc(sketch, "E17.2.3.3", {"start": v(-1.59, -11.11) * mm, "mid": v(-2.71, -11.58) * mm, "end": v(-3.17, -12.7) * mm});
            skLineSegment(sketch, "E17.2.3.4", {"start": v(-1.59, -11.11) * mm, "end": v(5.56, -11.11) * mm});
            skArc(sketch, "E17.2.3.5", {"start": v(7.14, -12.7) * mm, "mid": v(6.68, -11.58) * mm, "end": v(5.56, -11.11) * mm});
            skLineSegment(sketch, "E17.2.3.6", {"start": v(7.14, -12.7) * mm, "end": v(7.14, -19.05) * mm});
            skArc(sketch, "E17.2.3.7", {"start": v(5.56, -20.64) * mm, "mid": v(6.68, -20.17) * mm, "end": v(7.14, -19.05) * mm});
            skLineSegment(sketch, "E17.2.4.0", {"start": v(-1.59, -36.51) * mm, "end": v(5.56, -36.51) * mm});
            skArc(sketch, "E17.2.4.1", {"start": v(-3.17, -34.92) * mm, "mid": v(-2.71, -36.05) * mm, "end": v(-1.59, -36.51) * mm});
            skLineSegment(sketch, "E17.2.4.2", {"start": v(-3.17, -28.57) * mm, "end": v(-3.17, -34.92) * mm});
            skArc(sketch, "E17.2.4.3", {"start": v(-1.59, -26.99) * mm, "mid": v(-2.71, -27.45) * mm, "end": v(-3.17, -28.57) * mm});
            skLineSegment(sketch, "E17.2.4.4", {"start": v(-1.59, -26.99) * mm, "end": v(5.56, -26.99) * mm});
            skArc(sketch, "E17.2.4.5", {"start": v(7.14, -28.57) * mm, "mid": v(6.68, -27.45) * mm, "end": v(5.56, -26.99) * mm});
            skLineSegment(sketch, "E17.2.4.6", {"start": v(7.14, -28.57) * mm, "end": v(7.14, -34.92) * mm});
            skArc(sketch, "E17.2.4.7", {"start": v(5.56, -36.51) * mm, "mid": v(6.68, -36.05) * mm, "end": v(7.14, -34.92) * mm});
            skLineSegment(sketch, "E17.3.0.0", {"start": v(-20.64, 26.99) * mm, "end": v(-13.5, 26.99) * mm});
            skArc(sketch, "E17.3.0.1", {"start": v(-22.23, 28.58) * mm, "mid": v(-21.76, 27.45) * mm, "end": v(-20.64, 26.99) * mm});
            skLineSegment(sketch, "E17.3.0.2", {"start": v(-22.23, 34.93) * mm, "end": v(-22.23, 28.58) * mm});
            skArc(sketch, "E17.3.0.3", {"start": v(-20.64, 36.51) * mm, "mid": v(-21.76, 36.05) * mm, "end": v(-22.23, 34.93) * mm});
            skLineSegment(sketch, "E17.3.0.4", {"start": v(-20.64, 36.51) * mm, "end": v(-13.5, 36.51) * mm});
            skArc(sketch, "E17.3.0.5", {"start": v(-11.9, 34.93) * mm, "mid": v(-12.37, 36.05) * mm, "end": v(-13.5, 36.51) * mm});
            skLineSegment(sketch, "E17.3.0.6", {"start": v(-11.9, 34.93) * mm, "end": v(-11.9, 28.58) * mm});
            skArc(sketch, "E17.3.0.7", {"start": v(-13.5, 26.99) * mm, "mid": v(-12.37, 27.45) * mm, "end": v(-11.9, 28.58) * mm});
            skLineSegment(sketch, "E17.3.1.0", {"start": v(-20.64, 11.11) * mm, "end": v(-13.5, 11.11) * mm});
            skArc(sketch, "E17.3.1.1", {"start": v(-22.23, 12.7) * mm, "mid": v(-21.76, 11.58) * mm, "end": v(-20.64, 11.11) * mm});
            skLineSegment(sketch, "E17.3.1.2", {"start": v(-22.23, 19.05) * mm, "end": v(-22.23, 12.7) * mm});
            skArc(sketch, "E17.3.1.3", {"start": v(-20.64, 20.64) * mm, "mid": v(-21.76, 20.17) * mm, "end": v(-22.23, 19.05) * mm});
            skLineSegment(sketch, "E17.3.1.4", {"start": v(-20.64, 20.64) * mm, "end": v(-13.5, 20.64) * mm});
            skArc(sketch, "E17.3.1.5", {"start": v(-11.9, 19.05) * mm, "mid": v(-12.37, 20.17) * mm, "end": v(-13.5, 20.64) * mm});
            skLineSegment(sketch, "E17.3.1.6", {"start": v(-11.9, 19.05) * mm, "end": v(-11.9, 12.7) * mm});
            skArc(sketch, "E17.3.1.7", {"start": v(-13.5, 11.11) * mm, "mid": v(-12.37, 11.58) * mm, "end": v(-11.9, 12.7) * mm});
            skLineSegment(sketch, "E17.3.2.0", {"start": v(-20.64, -4.76) * mm, "end": v(-13.5, -4.76) * mm});
            skArc(sketch, "E17.3.2.1", {"start": v(-22.23, -3.17) * mm, "mid": v(-21.76, -4.3) * mm, "end": v(-20.64, -4.76) * mm});
            skLineSegment(sketch, "E17.3.2.2", {"start": v(-22.23, 3.18) * mm, "end": v(-22.23, -3.17) * mm});
            skArc(sketch, "E17.3.2.3", {"start": v(-20.64, 4.76) * mm, "mid": v(-21.76, 4.3) * mm, "end": v(-22.23, 3.18) * mm});
            skLineSegment(sketch, "E17.3.2.4", {"start": v(-20.64, 4.76) * mm, "end": v(-13.5, 4.76) * mm});
            skArc(sketch, "E17.3.2.5", {"start": v(-11.9, 3.18) * mm, "mid": v(-12.37, 4.3) * mm, "end": v(-13.5, 4.76) * mm});
            skLineSegment(sketch, "E17.3.2.6", {"start": v(-11.9, 3.18) * mm, "end": v(-11.9, -3.17) * mm});
            skArc(sketch, "E17.3.2.7", {"start": v(-13.5, -4.76) * mm, "mid": v(-12.37, -4.3) * mm, "end": v(-11.9, -3.17) * mm});
            skLineSegment(sketch, "E17.3.3.0", {"start": v(-20.64, -20.64) * mm, "end": v(-13.5, -20.64) * mm});
            skArc(sketch, "E17.3.3.1", {"start": v(-22.23, -19.05) * mm, "mid": v(-21.76, -20.17) * mm, "end": v(-20.64, -20.64) * mm});
            skLineSegment(sketch, "E17.3.3.2", {"start": v(-22.23, -12.7) * mm, "end": v(-22.23, -19.05) * mm});
            skArc(sketch, "E17.3.3.3", {"start": v(-20.64, -11.11) * mm, "mid": v(-21.76, -11.58) * mm, "end": v(-22.23, -12.7) * mm});
            skLineSegment(sketch, "E17.3.3.4", {"start": v(-20.64, -11.11) * mm, "end": v(-13.5, -11.11) * mm});
            skArc(sketch, "E17.3.3.5", {"start": v(-11.9, -12.7) * mm, "mid": v(-12.37, -11.58) * mm, "end": v(-13.5, -11.11) * mm});
            skLineSegment(sketch, "E17.3.3.6", {"start": v(-11.9, -12.7) * mm, "end": v(-11.9, -19.05) * mm});
            skArc(sketch, "E17.3.3.7", {"start": v(-13.5, -20.64) * mm, "mid": v(-12.37, -20.17) * mm, "end": v(-11.9, -19.05) * mm});
            skLineSegment(sketch, "E17.3.4.0", {"start": v(-20.64, -36.51) * mm, "end": v(-13.5, -36.51) * mm});
            skArc(sketch, "E17.3.4.1", {"start": v(-22.23, -34.92) * mm, "mid": v(-21.76, -36.05) * mm, "end": v(-20.64, -36.51) * mm});
            skLineSegment(sketch, "E17.3.4.2", {"start": v(-22.23, -28.57) * mm, "end": v(-22.23, -34.92) * mm});
            skArc(sketch, "E17.3.4.3", {"start": v(-20.64, -26.99) * mm, "mid": v(-21.76, -27.45) * mm, "end": v(-22.23, -28.57) * mm});
            skLineSegment(sketch, "E17.3.4.4", {"start": v(-20.64, -26.99) * mm, "end": v(-13.5, -26.99) * mm});
            skArc(sketch, "E17.3.4.5", {"start": v(-11.9, -28.57) * mm, "mid": v(-12.37, -27.45) * mm, "end": v(-13.5, -26.99) * mm});
            skLineSegment(sketch, "E17.3.4.6", {"start": v(-11.9, -28.57) * mm, "end": v(-11.9, -34.92) * mm});
            skArc(sketch, "E17.3.4.7", {"start": v(-13.5, -36.51) * mm, "mid": v(-12.37, -36.05) * mm, "end": v(-11.9, -34.92) * mm});
            skLineSegment(sketch, "E17.direction1", {"start": v(36.51, 26.99) * mm, "end": v(17.46, 26.99) * mm, "construction": true});
            skLineSegment(sketch, "E17.direction2", {"start": v(36.51, 26.99) * mm, "end": v(36.51, 11.11) * mm, "construction": true});
            skLineSegment(sketch, "E18.0.0", {"start": v(-53.98, 45.24) * mm, "end": v(53.98, 45.24) * mm});
            skLineSegment(sketch, "E18.0.1", {"start": v(53.98, 45.24) * mm, "end": v(53.98, -45.24) * mm});
            skLineSegment(sketch, "E18.0.2", {"start": v(53.98, -45.24) * mm, "end": v(-53.97, -45.24) * mm});
            skLineSegment(sketch, "E18.0.3", {"start": v(-53.97, -45.24) * mm, "end": v(-53.98, 45.24) * mm});
            skSolve(sketch);
        }
        {
            var Q0;
            Q0=makeQuery(id+"F1.opExtrude","CAP_FACE",FACE,{"disambiguationData":[OSD([sQuery(id+"F0.wireOp",EDGE,"E0.bottom"),sQuery(id+"F0.wireOp",EDGE,"E0.top"),sQuery(id+"F0.wireOp",EDGE,"E0.left"),sQuery(id+"F0.wireOp",EDGE,"E0.right")])],"isStart":false});
            var sketch = newSketch(context, id + "F7", { "sketchPlane" : qUnion([Q0])});
            skLineSegment(sketch, "E19.0", {"start": v(36.51, -26.99) * mm, "end": v(43.66, -26.99) * mm});
            skArc(sketch, "E20.0", {"start": v(34.93, -28.58) * mm, "mid": v(35.39, -27.45) * mm, "end": v(36.51, -26.99) * mm});
            skLineSegment(sketch, "E21.0", {"start": v(34.93, -34.93) * mm, "end": v(34.93, -28.58) * mm});
            skArc(sketch, "E22.0", {"start": v(36.51, -36.51) * mm, "mid": v(35.39, -36.05) * mm, "end": v(34.93, -34.93) * mm});
            skLineSegment(sketch, "E23.0", {"start": v(36.51, -36.51) * mm, "end": v(43.66, -36.51) * mm});
            skArc(sketch, "E24.0", {"start": v(45.24, -34.93) * mm, "mid": v(44.78, -36.05) * mm, "end": v(43.66, -36.51) * mm});
            skLineSegment(sketch, "E25.0", {"start": v(45.24, -34.93) * mm, "end": v(45.24, -28.58) * mm});
            skArc(sketch, "E26.0", {"start": v(43.66, -26.99) * mm, "mid": v(44.78, -27.45) * mm, "end": v(45.24, -28.58) * mm});
            skLineSegment(sketch, "E27.0.1.0", {"start": v(36.51, -11.11) * mm, "end": v(43.66, -11.11) * mm});
            skArc(sketch, "E27.0.1.1", {"start": v(34.93, -12.7) * mm, "mid": v(35.39, -11.58) * mm, "end": v(36.51, -11.11) * mm});
            skLineSegment(sketch, "E27.0.1.2", {"start": v(34.93, -19.05) * mm, "end": v(34.93, -12.7) * mm});
            skArc(sketch, "E27.0.1.3", {"start": v(36.51, -20.64) * mm, "mid": v(35.39, -20.17) * mm, "end": v(34.93, -19.05) * mm});
            skLineSegment(sketch, "E27.0.1.4", {"start": v(36.51, -20.64) * mm, "end": v(43.66, -20.64) * mm});
            skArc(sketch, "E27.0.1.5", {"start": v(45.24, -19.05) * mm, "mid": v(44.78, -20.17) * mm, "end": v(43.66, -20.64) * mm});
            skLineSegment(sketch, "E27.0.1.6", {"start": v(45.24, -19.05) * mm, "end": v(45.24, -12.7) * mm});
            skArc(sketch, "E27.0.1.7", {"start": v(43.66, -11.11) * mm, "mid": v(44.78, -11.58) * mm, "end": v(45.24, -12.7) * mm});
            skLineSegment(sketch, "E27.0.2.0", {"start": v(36.51, 4.76) * mm, "end": v(43.66, 4.76) * mm});
            skArc(sketch, "E27.0.2.1", {"start": v(34.93, 3.17) * mm, "mid": v(35.39, 4.3) * mm, "end": v(36.51, 4.76) * mm});
            skLineSegment(sketch, "E27.0.2.2", {"start": v(34.93, -3.18) * mm, "end": v(34.93, 3.17) * mm});
            skArc(sketch, "E27.0.2.3", {"start": v(36.51, -4.76) * mm, "mid": v(35.39, -4.3) * mm, "end": v(34.93, -3.18) * mm});
            skLineSegment(sketch, "E27.0.2.4", {"start": v(36.51, -4.76) * mm, "end": v(43.66, -4.76) * mm});
            skArc(sketch, "E27.0.2.5", {"start": v(45.24, -3.18) * mm, "mid": v(44.78, -4.3) * mm, "end": v(43.66, -4.76) * mm});
            skLineSegment(sketch, "E27.0.2.6", {"start": v(45.24, -3.18) * mm, "end": v(45.24, 3.17) * mm});
            skArc(sketch, "E27.0.2.7", {"start": v(43.66, 4.76) * mm, "mid": v(44.78, 4.3) * mm, "end": v(45.24, 3.17) * mm});
            skLineSegment(sketch, "E27.0.3.0", {"start": v(36.51, 20.64) * mm, "end": v(43.66, 20.64) * mm});
            skArc(sketch, "E27.0.3.1", {"start": v(34.93, 19.05) * mm, "mid": v(35.39, 20.17) * mm, "end": v(36.51, 20.64) * mm});
            skLineSegment(sketch, "E27.0.3.2", {"start": v(34.93, 12.7) * mm, "end": v(34.93, 19.05) * mm});
            skArc(sketch, "E27.0.3.3", {"start": v(36.51, 11.11) * mm, "mid": v(35.39, 11.58) * mm, "end": v(34.93, 12.7) * mm});
            skLineSegment(sketch, "E27.0.3.4", {"start": v(36.51, 11.11) * mm, "end": v(43.66, 11.11) * mm});
            skArc(sketch, "E27.0.3.5", {"start": v(45.24, 12.7) * mm, "mid": v(44.78, 11.58) * mm, "end": v(43.66, 11.11) * mm});
            skLineSegment(sketch, "E27.0.3.6", {"start": v(45.24, 12.7) * mm, "end": v(45.24, 19.05) * mm});
            skArc(sketch, "E27.0.3.7", {"start": v(43.66, 20.64) * mm, "mid": v(44.78, 20.17) * mm, "end": v(45.24, 19.05) * mm});
            skLineSegment(sketch, "E27.0.4.0", {"start": v(36.51, 36.51) * mm, "end": v(43.66, 36.51) * mm});
            skArc(sketch, "E27.0.4.1", {"start": v(34.93, 34.92) * mm, "mid": v(35.39, 36.05) * mm, "end": v(36.51, 36.51) * mm});
            skLineSegment(sketch, "E27.0.4.2", {"start": v(34.93, 28.57) * mm, "end": v(34.93, 34.92) * mm});
            skArc(sketch, "E27.0.4.3", {"start": v(36.51, 26.99) * mm, "mid": v(35.39, 27.45) * mm, "end": v(34.93, 28.57) * mm});
            skLineSegment(sketch, "E27.0.4.4", {"start": v(36.51, 26.99) * mm, "end": v(43.66, 26.99) * mm});
            skArc(sketch, "E27.0.4.5", {"start": v(45.24, 28.57) * mm, "mid": v(44.78, 27.45) * mm, "end": v(43.66, 26.99) * mm});
            skLineSegment(sketch, "E27.0.4.6", {"start": v(45.24, 28.57) * mm, "end": v(45.24, 34.92) * mm});
            skArc(sketch, "E27.0.4.7", {"start": v(43.66, 36.51) * mm, "mid": v(44.78, 36.05) * mm, "end": v(45.24, 34.92) * mm});
            skLineSegment(sketch, "E27.1.0.0", {"start": v(17.46, -26.99) * mm, "end": v(24.6, -26.99) * mm});
            skArc(sketch, "E27.1.0.1", {"start": v(15.88, -28.58) * mm, "mid": v(16.34, -27.45) * mm, "end": v(17.46, -26.99) * mm});
            skLineSegment(sketch, "E27.1.0.2", {"start": v(15.88, -34.93) * mm, "end": v(15.88, -28.58) * mm});
            skArc(sketch, "E27.1.0.3", {"start": v(17.46, -36.51) * mm, "mid": v(16.34, -36.05) * mm, "end": v(15.88, -34.93) * mm});
            skLineSegment(sketch, "E27.1.0.4", {"start": v(17.46, -36.51) * mm, "end": v(24.6, -36.51) * mm});
            skArc(sketch, "E27.1.0.5", {"start": v(26.2, -34.93) * mm, "mid": v(25.73, -36.05) * mm, "end": v(24.6, -36.51) * mm});
            skLineSegment(sketch, "E27.1.0.6", {"start": v(26.2, -34.93) * mm, "end": v(26.2, -28.58) * mm});
            skArc(sketch, "E27.1.0.7", {"start": v(24.6, -26.99) * mm, "mid": v(25.73, -27.45) * mm, "end": v(26.2, -28.58) * mm});
            skLineSegment(sketch, "E27.1.1.0", {"start": v(17.46, -11.11) * mm, "end": v(24.6, -11.11) * mm});
            skArc(sketch, "E27.1.1.1", {"start": v(15.88, -12.7) * mm, "mid": v(16.34, -11.58) * mm, "end": v(17.46, -11.11) * mm});
            skLineSegment(sketch, "E27.1.1.2", {"start": v(15.88, -19.05) * mm, "end": v(15.88, -12.7) * mm});
            skArc(sketch, "E27.1.1.3", {"start": v(17.46, -20.64) * mm, "mid": v(16.34, -20.17) * mm, "end": v(15.88, -19.05) * mm});
            skLineSegment(sketch, "E27.1.1.4", {"start": v(17.46, -20.64) * mm, "end": v(24.6, -20.64) * mm});
            skArc(sketch, "E27.1.1.5", {"start": v(26.2, -19.05) * mm, "mid": v(25.73, -20.17) * mm, "end": v(24.6, -20.64) * mm});
            skLineSegment(sketch, "E27.1.1.6", {"start": v(26.2, -19.05) * mm, "end": v(26.2, -12.7) * mm});
            skArc(sketch, "E27.1.1.7", {"start": v(24.6, -11.11) * mm, "mid": v(25.73, -11.58) * mm, "end": v(26.2, -12.7) * mm});
            skLineSegment(sketch, "E27.1.2.0", {"start": v(17.46, 4.76) * mm, "end": v(24.6, 4.76) * mm});
            skArc(sketch, "E27.1.2.1", {"start": v(15.88, 3.17) * mm, "mid": v(16.34, 4.3) * mm, "end": v(17.46, 4.76) * mm});
            skLineSegment(sketch, "E27.1.2.2", {"start": v(15.88, -3.18) * mm, "end": v(15.88, 3.17) * mm});
            skArc(sketch, "E27.1.2.3", {"start": v(17.46, -4.76) * mm, "mid": v(16.34, -4.3) * mm, "end": v(15.88, -3.18) * mm});
            skLineSegment(sketch, "E27.1.2.4", {"start": v(17.46, -4.76) * mm, "end": v(24.6, -4.76) * mm});
            skArc(sketch, "E27.1.2.5", {"start": v(26.2, -3.18) * mm, "mid": v(25.73, -4.3) * mm, "end": v(24.6, -4.76) * mm});
            skLineSegment(sketch, "E27.1.2.6", {"start": v(26.2, -3.18) * mm, "end": v(26.2, 3.17) * mm});
            skArc(sketch, "E27.1.2.7", {"start": v(24.6, 4.76) * mm, "mid": v(25.73, 4.3) * mm, "end": v(26.2, 3.17) * mm});
            skLineSegment(sketch, "E27.1.3.0", {"start": v(17.46, 20.64) * mm, "end": v(24.6, 20.64) * mm});
            skArc(sketch, "E27.1.3.1", {"start": v(15.88, 19.05) * mm, "mid": v(16.34, 20.17) * mm, "end": v(17.46, 20.64) * mm});
            skLineSegment(sketch, "E27.1.3.2", {"start": v(15.88, 12.7) * mm, "end": v(15.88, 19.05) * mm});
            skArc(sketch, "E27.1.3.3", {"start": v(17.46, 11.11) * mm, "mid": v(16.34, 11.58) * mm, "end": v(15.88, 12.7) * mm});
            skLineSegment(sketch, "E27.1.3.4", {"start": v(17.46, 11.11) * mm, "end": v(24.6, 11.11) * mm});
            skArc(sketch, "E27.1.3.5", {"start": v(26.2, 12.7) * mm, "mid": v(25.73, 11.58) * mm, "end": v(24.6, 11.11) * mm});
            skLineSegment(sketch, "E27.1.3.6", {"start": v(26.2, 12.7) * mm, "end": v(26.2, 19.05) * mm});
            skArc(sketch, "E27.1.3.7", {"start": v(24.6, 20.64) * mm, "mid": v(25.73, 20.17) * mm, "end": v(26.2, 19.05) * mm});
            skLineSegment(sketch, "E27.1.4.0", {"start": v(17.46, 36.51) * mm, "end": v(24.6, 36.51) * mm});
            skArc(sketch, "E27.1.4.1", {"start": v(15.88, 34.92) * mm, "mid": v(16.34, 36.05) * mm, "end": v(17.46, 36.51) * mm});
            skLineSegment(sketch, "E27.1.4.2", {"start": v(15.88, 28.57) * mm, "end": v(15.88, 34.92) * mm});
            skArc(sketch, "E27.1.4.3", {"start": v(17.46, 26.99) * mm, "mid": v(16.34, 27.45) * mm, "end": v(15.88, 28.57) * mm});
            skLineSegment(sketch, "E27.1.4.4", {"start": v(17.46, 26.99) * mm, "end": v(24.6, 26.99) * mm});
            skArc(sketch, "E27.1.4.5", {"start": v(26.2, 28.57) * mm, "mid": v(25.73, 27.45) * mm, "end": v(24.6, 26.99) * mm});
            skLineSegment(sketch, "E27.1.4.6", {"start": v(26.2, 28.57) * mm, "end": v(26.2, 34.92) * mm});
            skArc(sketch, "E27.1.4.7", {"start": v(24.6, 36.51) * mm, "mid": v(25.73, 36.05) * mm, "end": v(26.2, 34.92) * mm});
            skLineSegment(sketch, "E27.2.0.0", {"start": v(-1.59, -26.99) * mm, "end": v(5.56, -26.99) * mm});
            skArc(sketch, "E27.2.0.1", {"start": v(-3.17, -28.58) * mm, "mid": v(-2.71, -27.45) * mm, "end": v(-1.59, -26.99) * mm});
            skLineSegment(sketch, "E27.2.0.2", {"start": v(-3.17, -34.93) * mm, "end": v(-3.17, -28.58) * mm});
            skArc(sketch, "E27.2.0.3", {"start": v(-1.59, -36.51) * mm, "mid": v(-2.71, -36.05) * mm, "end": v(-3.17, -34.93) * mm});
            skLineSegment(sketch, "E27.2.0.4", {"start": v(-1.59, -36.51) * mm, "end": v(5.56, -36.51) * mm});
            skArc(sketch, "E27.2.0.5", {"start": v(7.14, -34.93) * mm, "mid": v(6.68, -36.05) * mm, "end": v(5.56, -36.51) * mm});
            skLineSegment(sketch, "E27.2.0.6", {"start": v(7.14, -34.93) * mm, "end": v(7.14, -28.58) * mm});
            skArc(sketch, "E27.2.0.7", {"start": v(5.56, -26.99) * mm, "mid": v(6.68, -27.45) * mm, "end": v(7.14, -28.58) * mm});
            skLineSegment(sketch, "E27.2.1.0", {"start": v(-1.59, -11.11) * mm, "end": v(5.56, -11.11) * mm});
            skArc(sketch, "E27.2.1.1", {"start": v(-3.17, -12.7) * mm, "mid": v(-2.71, -11.58) * mm, "end": v(-1.59, -11.11) * mm});
            skLineSegment(sketch, "E27.2.1.2", {"start": v(-3.17, -19.05) * mm, "end": v(-3.17, -12.7) * mm});
            skArc(sketch, "E27.2.1.3", {"start": v(-1.59, -20.64) * mm, "mid": v(-2.71, -20.17) * mm, "end": v(-3.17, -19.05) * mm});
            skLineSegment(sketch, "E27.2.1.4", {"start": v(-1.59, -20.64) * mm, "end": v(5.56, -20.64) * mm});
            skArc(sketch, "E27.2.1.5", {"start": v(7.14, -19.05) * mm, "mid": v(6.68, -20.17) * mm, "end": v(5.56, -20.64) * mm});
            skLineSegment(sketch, "E27.2.1.6", {"start": v(7.14, -19.05) * mm, "end": v(7.14, -12.7) * mm});
            skArc(sketch, "E27.2.1.7", {"start": v(5.56, -11.11) * mm, "mid": v(6.68, -11.58) * mm, "end": v(7.14, -12.7) * mm});
            skLineSegment(sketch, "E27.2.2.0", {"start": v(-1.59, 4.76) * mm, "end": v(5.56, 4.76) * mm});
            skArc(sketch, "E27.2.2.1", {"start": v(-3.17, 3.17) * mm, "mid": v(-2.71, 4.3) * mm, "end": v(-1.59, 4.76) * mm});
            skLineSegment(sketch, "E27.2.2.2", {"start": v(-3.17, -3.18) * mm, "end": v(-3.17, 3.17) * mm});
            skArc(sketch, "E27.2.2.3", {"start": v(-1.59, -4.76) * mm, "mid": v(-2.71, -4.3) * mm, "end": v(-3.17, -3.18) * mm});
            skLineSegment(sketch, "E27.2.2.4", {"start": v(-1.59, -4.76) * mm, "end": v(5.56, -4.76) * mm});
            skArc(sketch, "E27.2.2.5", {"start": v(7.14, -3.18) * mm, "mid": v(6.68, -4.3) * mm, "end": v(5.56, -4.76) * mm});
            skLineSegment(sketch, "E27.2.2.6", {"start": v(7.14, -3.18) * mm, "end": v(7.14, 3.17) * mm});
            skArc(sketch, "E27.2.2.7", {"start": v(5.56, 4.76) * mm, "mid": v(6.68, 4.3) * mm, "end": v(7.14, 3.17) * mm});
            skLineSegment(sketch, "E27.2.3.0", {"start": v(-1.59, 20.64) * mm, "end": v(5.56, 20.64) * mm});
            skArc(sketch, "E27.2.3.1", {"start": v(-3.17, 19.05) * mm, "mid": v(-2.71, 20.17) * mm, "end": v(-1.59, 20.64) * mm});
            skLineSegment(sketch, "E27.2.3.2", {"start": v(-3.17, 12.7) * mm, "end": v(-3.17, 19.05) * mm});
            skArc(sketch, "E27.2.3.3", {"start": v(-1.59, 11.11) * mm, "mid": v(-2.71, 11.58) * mm, "end": v(-3.17, 12.7) * mm});
            skLineSegment(sketch, "E27.2.3.4", {"start": v(-1.59, 11.11) * mm, "end": v(5.56, 11.11) * mm});
            skArc(sketch, "E27.2.3.5", {"start": v(7.14, 12.7) * mm, "mid": v(6.68, 11.58) * mm, "end": v(5.56, 11.11) * mm});
            skLineSegment(sketch, "E27.2.3.6", {"start": v(7.14, 12.7) * mm, "end": v(7.14, 19.05) * mm});
            skArc(sketch, "E27.2.3.7", {"start": v(5.56, 20.64) * mm, "mid": v(6.68, 20.17) * mm, "end": v(7.14, 19.05) * mm});
            skLineSegment(sketch, "E27.2.4.0", {"start": v(-1.59, 36.51) * mm, "end": v(5.56, 36.51) * mm});
            skArc(sketch, "E27.2.4.1", {"start": v(-3.17, 34.92) * mm, "mid": v(-2.71, 36.05) * mm, "end": v(-1.59, 36.51) * mm});
            skLineSegment(sketch, "E27.2.4.2", {"start": v(-3.17, 28.57) * mm, "end": v(-3.17, 34.92) * mm});
            skArc(sketch, "E27.2.4.3", {"start": v(-1.59, 26.99) * mm, "mid": v(-2.71, 27.45) * mm, "end": v(-3.17, 28.57) * mm});
            skLineSegment(sketch, "E27.2.4.4", {"start": v(-1.59, 26.99) * mm, "end": v(5.56, 26.99) * mm});
            skArc(sketch, "E27.2.4.5", {"start": v(7.14, 28.57) * mm, "mid": v(6.68, 27.45) * mm, "end": v(5.56, 26.99) * mm});
            skLineSegment(sketch, "E27.2.4.6", {"start": v(7.14, 28.57) * mm, "end": v(7.14, 34.92) * mm});
            skArc(sketch, "E27.2.4.7", {"start": v(5.56, 36.51) * mm, "mid": v(6.68, 36.05) * mm, "end": v(7.14, 34.92) * mm});
            skLineSegment(sketch, "E27.3.0.0", {"start": v(-20.64, -26.99) * mm, "end": v(-13.5, -26.99) * mm});
            skArc(sketch, "E27.3.0.1", {"start": v(-22.23, -28.58) * mm, "mid": v(-21.76, -27.45) * mm, "end": v(-20.64, -26.99) * mm});
            skLineSegment(sketch, "E27.3.0.2", {"start": v(-22.23, -34.93) * mm, "end": v(-22.23, -28.58) * mm});
            skArc(sketch, "E27.3.0.3", {"start": v(-20.64, -36.51) * mm, "mid": v(-21.76, -36.05) * mm, "end": v(-22.23, -34.93) * mm});
            skLineSegment(sketch, "E27.3.0.4", {"start": v(-20.64, -36.51) * mm, "end": v(-13.5, -36.51) * mm});
            skArc(sketch, "E27.3.0.5", {"start": v(-11.9, -34.93) * mm, "mid": v(-12.37, -36.05) * mm, "end": v(-13.5, -36.51) * mm});
            skLineSegment(sketch, "E27.3.0.6", {"start": v(-11.9, -34.93) * mm, "end": v(-11.9, -28.58) * mm});
            skArc(sketch, "E27.3.0.7", {"start": v(-13.5, -26.99) * mm, "mid": v(-12.37, -27.45) * mm, "end": v(-11.9, -28.58) * mm});
            skLineSegment(sketch, "E27.3.1.0", {"start": v(-20.64, -11.11) * mm, "end": v(-13.5, -11.11) * mm});
            skArc(sketch, "E27.3.1.1", {"start": v(-22.23, -12.7) * mm, "mid": v(-21.76, -11.58) * mm, "end": v(-20.64, -11.11) * mm});
            skLineSegment(sketch, "E27.3.1.2", {"start": v(-22.23, -19.05) * mm, "end": v(-22.23, -12.7) * mm});
            skArc(sketch, "E27.3.1.3", {"start": v(-20.64, -20.64) * mm, "mid": v(-21.76, -20.17) * mm, "end": v(-22.23, -19.05) * mm});
            skLineSegment(sketch, "E27.3.1.4", {"start": v(-20.64, -20.64) * mm, "end": v(-13.5, -20.64) * mm});
            skArc(sketch, "E27.3.1.5", {"start": v(-11.9, -19.05) * mm, "mid": v(-12.37, -20.17) * mm, "end": v(-13.5, -20.64) * mm});
            skLineSegment(sketch, "E27.3.1.6", {"start": v(-11.9, -19.05) * mm, "end": v(-11.9, -12.7) * mm});
            skArc(sketch, "E27.3.1.7", {"start": v(-13.5, -11.11) * mm, "mid": v(-12.37, -11.58) * mm, "end": v(-11.9, -12.7) * mm});
            skLineSegment(sketch, "E27.3.2.0", {"start": v(-20.64, 4.76) * mm, "end": v(-13.5, 4.76) * mm});
            skArc(sketch, "E27.3.2.1", {"start": v(-22.23, 3.17) * mm, "mid": v(-21.76, 4.3) * mm, "end": v(-20.64, 4.76) * mm});
            skLineSegment(sketch, "E27.3.2.2", {"start": v(-22.23, -3.18) * mm, "end": v(-22.23, 3.17) * mm});
            skArc(sketch, "E27.3.2.3", {"start": v(-20.64, -4.76) * mm, "mid": v(-21.76, -4.3) * mm, "end": v(-22.23, -3.18) * mm});
            skLineSegment(sketch, "E27.3.2.4", {"start": v(-20.64, -4.76) * mm, "end": v(-13.5, -4.76) * mm});
            skArc(sketch, "E27.3.2.5", {"start": v(-11.9, -3.18) * mm, "mid": v(-12.37, -4.3) * mm, "end": v(-13.5, -4.76) * mm});
            skLineSegment(sketch, "E27.3.2.6", {"start": v(-11.9, -3.18) * mm, "end": v(-11.9, 3.17) * mm});
            skArc(sketch, "E27.3.2.7", {"start": v(-13.5, 4.76) * mm, "mid": v(-12.37, 4.3) * mm, "end": v(-11.9, 3.17) * mm});
            skLineSegment(sketch, "E27.3.3.0", {"start": v(-20.64, 20.64) * mm, "end": v(-13.5, 20.64) * mm});
            skArc(sketch, "E27.3.3.1", {"start": v(-22.23, 19.05) * mm, "mid": v(-21.76, 20.17) * mm, "end": v(-20.64, 20.64) * mm});
            skLineSegment(sketch, "E27.3.3.2", {"start": v(-22.23, 12.7) * mm, "end": v(-22.23, 19.05) * mm});
            skArc(sketch, "E27.3.3.3", {"start": v(-20.64, 11.11) * mm, "mid": v(-21.76, 11.58) * mm, "end": v(-22.23, 12.7) * mm});
            skLineSegment(sketch, "E27.3.3.4", {"start": v(-20.64, 11.11) * mm, "end": v(-13.5, 11.11) * mm});
            skArc(sketch, "E27.3.3.5", {"start": v(-11.9, 12.7) * mm, "mid": v(-12.37, 11.58) * mm, "end": v(-13.5, 11.11) * mm});
            skLineSegment(sketch, "E27.3.3.6", {"start": v(-11.9, 12.7) * mm, "end": v(-11.9, 19.05) * mm});
            skArc(sketch, "E27.3.3.7", {"start": v(-13.5, 20.64) * mm, "mid": v(-12.37, 20.17) * mm, "end": v(-11.9, 19.05) * mm});
            skLineSegment(sketch, "E27.3.4.0", {"start": v(-20.64, 36.51) * mm, "end": v(-13.5, 36.51) * mm});
            skArc(sketch, "E27.3.4.1", {"start": v(-22.23, 34.92) * mm, "mid": v(-21.76, 36.05) * mm, "end": v(-20.64, 36.51) * mm});
            skLineSegment(sketch, "E27.3.4.2", {"start": v(-22.23, 28.57) * mm, "end": v(-22.23, 34.92) * mm});
            skArc(sketch, "E27.3.4.3", {"start": v(-20.64, 26.99) * mm, "mid": v(-21.76, 27.45) * mm, "end": v(-22.23, 28.57) * mm});
            skLineSegment(sketch, "E27.3.4.4", {"start": v(-20.64, 26.99) * mm, "end": v(-13.5, 26.99) * mm});
            skArc(sketch, "E27.3.4.5", {"start": v(-11.9, 28.57) * mm, "mid": v(-12.37, 27.45) * mm, "end": v(-13.5, 26.99) * mm});
            skLineSegment(sketch, "E27.3.4.6", {"start": v(-11.9, 28.57) * mm, "end": v(-11.9, 34.92) * mm});
            skArc(sketch, "E27.3.4.7", {"start": v(-13.5, 36.51) * mm, "mid": v(-12.37, 36.05) * mm, "end": v(-11.9, 34.92) * mm});
            skLineSegment(sketch, "E27.direction1", {"start": v(36.51, -26.99) * mm, "end": v(17.46, -26.99) * mm, "construction": true});
            skLineSegment(sketch, "E27.direction2", {"start": v(36.51, -26.99) * mm, "end": v(36.51, -11.11) * mm, "construction": true});
            skSolve(sketch);
        }
        {
            var Q0;
            Q0=makeQuery(id+"F7.imprint","IMPRINT",FACE,{"disambiguationData":[TD([[makeQuery(id+"F7.imprint","IMPRINT",EDGE,{"derivedFrom":sQuery(id+"F7.wireOp",EDGE,"E19.0")}),-1.0]])]});
            var Q1;
            Q1=makeQuery(id+"F7.imprint","IMPRINT",FACE,{"disambiguationData":[TD([[makeQuery(id+"F7.imprint","IMPRINT",EDGE,{"derivedFrom":sQuery(id+"F7.wireOp",EDGE,"E27.0.1.0")}),-1.0]])]});
            var Q2;
            Q2=makeQuery(id+"F7.imprint","IMPRINT",FACE,{"disambiguationData":[TD([[makeQuery(id+"F7.imprint","IMPRINT",EDGE,{"derivedFrom":sQuery(id+"F7.wireOp",EDGE,"E27.1.1.0")}),-1.0]])]});
            var Q3;
            Q3=makeQuery(id+"F7.imprint","IMPRINT",FACE,{"disambiguationData":[TD([[makeQuery(id+"F7.imprint","IMPRINT",EDGE,{"derivedFrom":sQuery(id+"F7.wireOp",EDGE,"E27.1.0.0")}),-1.0]])]});
            var Q4;
            Q4=makeQuery(id+"F7.imprint","IMPRINT",FACE,{"disambiguationData":[TD([[makeQuery(id+"F7.imprint","IMPRINT",EDGE,{"derivedFrom":sQuery(id+"F7.wireOp",EDGE,"E27.2.0.0")}),-1.0]])]});
            var Q5;
            Q5=makeQuery(id+"F7.imprint","IMPRINT",FACE,{"disambiguationData":[TD([[makeQuery(id+"F7.imprint","IMPRINT",EDGE,{"derivedFrom":sQuery(id+"F7.wireOp",EDGE,"E27.2.1.0")}),-1.0]])]});
            var Q6;
            Q6=makeQuery(id+"F7.imprint","IMPRINT",FACE,{"disambiguationData":[TD([[makeQuery(id+"F7.imprint","IMPRINT",EDGE,{"derivedFrom":sQuery(id+"F7.wireOp",EDGE,"E27.3.1.0")}),-1.0]])]});
            var Q7;
            Q7=makeQuery(id+"F7.imprint","IMPRINT",FACE,{"disambiguationData":[TD([[makeQuery(id+"F7.imprint","IMPRINT",EDGE,{"derivedFrom":sQuery(id+"F7.wireOp",EDGE,"E27.3.0.0")}),-1.0]])]});
            var Q8;
            Q8=makeQuery(id+"F7.imprint","IMPRINT",FACE,{"disambiguationData":[TD([[makeQuery(id+"F7.imprint","IMPRINT",EDGE,{"derivedFrom":sQuery(id+"F7.wireOp",EDGE,"E27.3.2.0")}),-1.0]])]});
            var Q9;
            Q9=makeQuery(id+"F7.imprint","IMPRINT",FACE,{"disambiguationData":[TD([[makeQuery(id+"F7.imprint","IMPRINT",EDGE,{"derivedFrom":sQuery(id+"F7.wireOp",EDGE,"E27.3.3.0")}),-1.0]])]});
            var Q10;
            Q10=makeQuery(id+"F7.imprint","IMPRINT",FACE,{"disambiguationData":[TD([[makeQuery(id+"F7.imprint","IMPRINT",EDGE,{"derivedFrom":sQuery(id+"F7.wireOp",EDGE,"E27.3.4.0")}),-1.0]])]});
            var Q11;
            Q11=makeQuery(id+"F7.imprint","IMPRINT",FACE,{"disambiguationData":[TD([[makeQuery(id+"F7.imprint","IMPRINT",EDGE,{"derivedFrom":sQuery(id+"F7.wireOp",EDGE,"E27.2.4.0")}),-1.0]])]});
            var Q12;
            Q12=makeQuery(id+"F7.imprint","IMPRINT",FACE,{"disambiguationData":[TD([[makeQuery(id+"F7.imprint","IMPRINT",EDGE,{"derivedFrom":sQuery(id+"F7.wireOp",EDGE,"E27.1.4.0")}),-1.0]])]});
            var Q13;
            Q13=makeQuery(id+"F7.imprint","IMPRINT",FACE,{"disambiguationData":[TD([[makeQuery(id+"F7.imprint","IMPRINT",EDGE,{"derivedFrom":sQuery(id+"F7.wireOp",EDGE,"E27.0.4.0")}),-1.0]])]});
            var Q14;
            Q14=makeQuery(id+"F7.imprint","IMPRINT",FACE,{"disambiguationData":[TD([[makeQuery(id+"F7.imprint","IMPRINT",EDGE,{"derivedFrom":sQuery(id+"F7.wireOp",EDGE,"E27.0.3.0")}),-1.0]])]});
            var Q15;
            Q15=makeQuery(id+"F7.imprint","IMPRINT",FACE,{"disambiguationData":[TD([[makeQuery(id+"F7.imprint","IMPRINT",EDGE,{"derivedFrom":sQuery(id+"F7.wireOp",EDGE,"E27.0.2.0")}),-1.0]])]});
            var Q16;
            Q16=makeQuery(id+"F7.imprint","IMPRINT",FACE,{"disambiguationData":[TD([[makeQuery(id+"F7.imprint","IMPRINT",EDGE,{"derivedFrom":sQuery(id+"F7.wireOp",EDGE,"E27.1.2.0")}),-1.0]])]});
            var Q17;
            Q17=makeQuery(id+"F7.imprint","IMPRINT",FACE,{"disambiguationData":[TD([[makeQuery(id+"F7.imprint","IMPRINT",EDGE,{"derivedFrom":sQuery(id+"F7.wireOp",EDGE,"E27.2.2.0")}),-1.0]])]});
            var Q18;
            Q18=makeQuery(id+"F7.imprint","IMPRINT",FACE,{"disambiguationData":[TD([[makeQuery(id+"F7.imprint","IMPRINT",EDGE,{"derivedFrom":sQuery(id+"F7.wireOp",EDGE,"E27.2.3.0")}),-1.0]])]});
            var Q19;
            Q19=makeQuery(id+"F7.imprint","IMPRINT",FACE,{"disambiguationData":[TD([[makeQuery(id+"F7.imprint","IMPRINT",EDGE,{"derivedFrom":sQuery(id+"F7.wireOp",EDGE,"E27.1.3.0")}),-1.0]])]});
            extrude(context, id + "F8", {"entities" : qUnion([Q0, Q1, Q2, Q3, Q4, Q5, Q6, Q7, Q8, Q9, Q10, Q11, Q12, Q13, Q14, Q15, Q16, Q17, Q18, Q19]), "operationType" : NewBodyOperationType.REMOVE, "oppositeDirection" : true, "depth" : 25.4 * mm});
        }
        {
            var Q0;
            Q0=makeQuery(id+"F1.opExtrude","SWEPT_FACE",FACE,{"disambiguationData":[OSD([sQuery(id+"F0.wireOp",EDGE,"E0.bottom")])]});
            var sketch = newSketch(context, id + "F9", { "sketchPlane" : qUnion([Q0])});
            skLineSegment(sketch, "E28.bottom", {"start": v(-46.04, 0) * mm, "end": v(-34.13, 0) * mm});
            skLineSegment(sketch, "E28.top", {"start": v(-46.04, 6.35) * mm, "end": v(-34.13, 6.35) * mm});
            skLineSegment(sketch, "E28.left", {"start": v(-46.04, 0) * mm, "end": v(-46.04, 6.35) * mm});
            skLineSegment(sketch, "E28.right", {"start": v(-34.13, 0) * mm, "end": v(-34.13, 6.35) * mm});
            skSolve(sketch);
        }
        {
            var Q0;
            Q0=makeQuery(id+"F9.imprint","IMPRINT",FACE,{"disambiguationData":[TD([[makeQuery(id+"F9.imprint","IMPRINT",EDGE,{"derivedFrom":sQuery(id+"F9.wireOp",EDGE,"E28.bottom")}),-1.0]])]});
            extrude(context, id + "F10", {"entities" : qUnion([Q0]), "operationType" : NewBodyOperationType.REMOVE, "oppositeDirection" : true, "depth" : 4.76 * mm});
        }
        {
            var Q0;
            Q0=makeQuery(id+"F1.opExtrude","CAP_EDGE",EDGE,{"disambiguationData":[OSD([sQuery(id+"F0.wireOp",EDGE,"E0.bottom")])],"isStart":false});
            var Q1;
            Q1=makeQuery(id+"F1.opExtrude","CAP_EDGE",EDGE,{"disambiguationData":[OSD([sQuery(id+"F0.wireOp",EDGE,"E0.right")])],"isStart":false});
            var Q2;
            Q2=makeQuery(id+"F1.opExtrude","CAP_EDGE",EDGE,{"disambiguationData":[OSD([sQuery(id+"F0.wireOp",EDGE,"E0.top")])],"isStart":false});
            var Q3;
            Q3=makeQuery(id+"F1.opExtrude","SWEPT_EDGE",EDGE,{"disambiguationData":[OSD([sQuery(id+"F0.wireOp",EDGE,"E0.top"),sQuery(id+"F0.wireOp",EDGE,"E0.right")])]});
            var Q4;
            Q4=makeQuery(id+"F1.opExtrude","SWEPT_EDGE",EDGE,{"disambiguationData":[OSD([sQuery(id+"F0.wireOp",EDGE,"E0.bottom"),sQuery(id+"F0.wireOp",EDGE,"E0.right")])]});
            var Q5;
            Q5=makeQuery(id+"F1.opExtrude","CAP_EDGE",EDGE,{"disambiguationData":[OSD([sQuery(id+"F0.wireOp",EDGE,"E0.left")])],"isStart":false});
            var Q6;
            Q6=makeQuery(id+"F1.opExtrude","SWEPT_EDGE",EDGE,{"disambiguationData":[OSD([sQuery(id+"F0.wireOp",EDGE,"E0.bottom"),sQuery(id+"F0.wireOp",EDGE,"E0.left")])]});
            var Q7;
            Q7=makeQuery(id+"F1.opExtrude","SWEPT_EDGE",EDGE,{"disambiguationData":[OSD([sQuery(id+"F0.wireOp",EDGE,"E0.top"),sQuery(id+"F0.wireOp",EDGE,"E0.left")])]});
            fillet(context, id + "F11", {"entities" : qUnion([Q0, Q1, Q2, Q3, Q4, Q5, Q6, Q7]), "radius" : 3.17 * mm, "tangentPropagation" : true, "allowEdgeOverflow" : false});
        }
        {
            var Q0;
            Q0=makeQuery(id+"F3.boolean.opBoolean","COPY",FACE,{"derivedFrom":makeQuery(id+"F3.opExtrude","CAP_FACE",FACE,{"disambiguationData":[OSD([sQuery(id+"F2.wireOp",EDGE,"E2.bottom"),sQuery(id+"F2.wireOp",EDGE,"E2.top"),sQuery(id+"F2.wireOp",EDGE,"E2.left"),sQuery(id+"F2.wireOp",EDGE,"E2.right")])],"isStart":false})});
            var sketch = newSketch(context, id + "F12", { "sketchPlane" : qUnion([Q0])});
            skLineSegment(sketch, "E29.0.0", {"start": v(-34.13, 40.48) * mm, "end": v(-46.04, 40.48) * mm});
            skLineSegment(sketch, "E29.0.1", {"start": v(-46.04, 40.48) * mm, "end": v(-46.04, 42.07) * mm});
            skLineSegment(sketch, "E29.0.2", {"start": v(-46.04, 42.07) * mm, "end": v(-50.8, 42.07) * mm});
            skLineSegment(sketch, "E29.0.3", {"start": v(-50.8, 42.07) * mm, "end": v(-50.8, -39.69) * mm});
            skLineSegment(sketch, "E29.0.4", {"start": v(-50.8, -39.69) * mm, "end": v(50.8, -39.69) * mm});
            skLineSegment(sketch, "E29.0.5", {"start": v(50.8, -39.69) * mm, "end": v(50.8, 42.07) * mm});
            skLineSegment(sketch, "E29.0.6", {"start": v(50.8, 42.07) * mm, "end": v(-34.13, 42.07) * mm});
            skLineSegment(sketch, "E29.0.7", {"start": v(-34.13, 42.07) * mm, "end": v(-34.13, 40.48) * mm});
            skLineSegment(sketch, "E30.bottom", {"start": v(-50.8, -39.69) * mm, "end": v(-45.88, -39.69) * mm});
            skLineSegment(sketch, "E30.top", {"start": v(-50.8, -34.37) * mm, "end": v(-45.88, -34.37) * mm});
            skLineSegment(sketch, "E30.left", {"start": v(-50.8, -39.69) * mm, "end": v(-50.8, -34.37) * mm});
            skLineSegment(sketch, "E30.right", {"start": v(-45.88, -39.69) * mm, "end": v(-45.88, -34.37) * mm});
            skLineSegment(sketch, "E31.0.0", {"start": v(53.98, -42.07) * mm, "end": v(53.98, 42.07) * mm});
            skArc(sketch, "E31.0.1", {"start": v(53.98, 42.07) * mm, "mid": v(53.05, 44.31) * mm, "end": v(50.8, 45.24) * mm});
            skLineSegment(sketch, "E31.0.2", {"start": v(50.8, 45.24) * mm, "end": v(-34.13, 45.24) * mm});
            skLineSegment(sketch, "E31.0.3", {"start": v(-34.13, 45.24) * mm, "end": v(-34.13, 42.07) * mm});
            skLineSegment(sketch, "E31.0.4", {"start": v(-34.13, 42.07) * mm, "end": v(50.8, 42.07) * mm});
            skLineSegment(sketch, "E31.0.5", {"start": v(50.8, 42.07) * mm, "end": v(50.8, -39.69) * mm});
            skLineSegment(sketch, "E31.0.6", {"start": v(50.8, -39.69) * mm, "end": v(-50.8, -39.69) * mm});
            skLineSegment(sketch, "E31.0.7", {"start": v(-50.8, -39.69) * mm, "end": v(-50.8, 42.07) * mm});
            skLineSegment(sketch, "E31.0.8", {"start": v(-50.8, 42.07) * mm, "end": v(-46.04, 42.07) * mm});
            skLineSegment(sketch, "E31.0.9", {"start": v(-46.04, 42.07) * mm, "end": v(-46.04, 45.24) * mm});
            skLineSegment(sketch, "E31.0.10", {"start": v(-46.04, 45.24) * mm, "end": v(-50.8, 45.24) * mm});
            skArc(sketch, "E31.0.11", {"start": v(-50.8, 45.24) * mm, "mid": v(-53.05, 44.31) * mm, "end": v(-53.98, 42.07) * mm});
            skLineSegment(sketch, "E31.0.12", {"start": v(-53.98, 42.07) * mm, "end": v(-53.98, -42.07) * mm});
            skArc(sketch, "E31.0.13", {"start": v(-53.98, -42.07) * mm, "mid": v(-53.05, -44.31) * mm, "end": v(-50.8, -45.24) * mm});
            skLineSegment(sketch, "E31.0.14", {"start": v(-50.8, -45.24) * mm, "end": v(50.8, -45.24) * mm});
            skArc(sketch, "E31.0.15", {"start": v(50.8, -45.24) * mm, "mid": v(53.05, -44.31) * mm, "end": v(53.98, -42.07) * mm});
            skLineSegment(sketch, "E32.bottom", {"start": v(50.8, -39.69) * mm, "end": v(46.35, -39.69) * mm});
            skLineSegment(sketch, "E32.left", {"start": v(50.8, -39.69) * mm, "end": v(50.8, -34.37) * mm});
            skLineSegment(sketch, "E33.bottom", {"start": v(50.8, -39.69) * mm, "end": v(48.82, -39.69) * mm});
            skLineSegment(sketch, "E33.left", {"start": v(50.8, -39.69) * mm, "end": v(50.8, -36.91) * mm});
            skLineSegment(sketch, "E34.bottom", {"start": v(50.8, -39.69) * mm, "end": v(47.62, -39.69) * mm});
            skLineSegment(sketch, "E34.top", {"start": v(50.8, -34.37) * mm, "end": v(47.62, -34.37) * mm});
            skLineSegment(sketch, "E34.right", {"start": v(47.62, -39.69) * mm, "end": v(47.62, -34.37) * mm});
            skLineSegment(sketch, "E35.bottom", {"start": v(50.8, 42.07) * mm, "end": v(47.62, 42.07) * mm});
            skLineSegment(sketch, "E35.top", {"start": v(50.8, 34.37) * mm, "end": v(47.62, 34.37) * mm});
            skLineSegment(sketch, "E35.left", {"start": v(50.8, 42.07) * mm, "end": v(50.8, 34.37) * mm});
            skLineSegment(sketch, "E35.right", {"start": v(47.62, 42.07) * mm, "end": v(47.62, 34.37) * mm});
            skSolve(sketch);
        }
        {
            var Q0;
            Q0=makeQuery(id+"F1.opExtrude","CAP_FACE",FACE,{"disambiguationData":[OSD([sQuery(id+"F0.wireOp",EDGE,"E0.bottom"),sQuery(id+"F0.wireOp",EDGE,"E0.top"),sQuery(id+"F0.wireOp",EDGE,"E0.left"),sQuery(id+"F0.wireOp",EDGE,"E0.right")])],"isStart":true});
            var sketch = newSketch(context, id + "F13", { "sketchPlane" : qUnion([Q0])});
            skLineSegment(sketch, "E36.0.0", {"start": v(-45.88, -34.37) * mm, "end": v(-50.8, -34.37) * mm});
            skLineSegment(sketch, "E36.0.1", {"start": v(-50.8, -34.37) * mm, "end": v(-50.8, -39.69) * mm});
            skLineSegment(sketch, "E36.0.2", {"start": v(-50.8, -39.69) * mm, "end": v(-45.88, -39.69) * mm});
            skLineSegment(sketch, "E36.0.3", {"start": v(-45.88, -39.69) * mm, "end": v(-45.88, -34.37) * mm});
            skLineSegment(sketch, "E37.0.0", {"start": v(50.8, -36.91) * mm, "end": v(50.8, -34.37) * mm});
            skLineSegment(sketch, "E37.0.1", {"start": v(50.8, -34.37) * mm, "end": v(47.62, -34.37) * mm});
            skLineSegment(sketch, "E37.0.2", {"start": v(47.62, -34.37) * mm, "end": v(47.62, -38.9) * mm});
            skLineSegment(sketch, "E37.0.3", {"start": v(47.62, -38.9) * mm, "end": v(47.62, -39.69) * mm});
            skLineSegment(sketch, "E37.0.4", {"start": v(47.62, -39.69) * mm, "end": v(48.82, -39.69) * mm});
            skLineSegment(sketch, "E37.0.5", {"start": v(48.82, -39.69) * mm, "end": v(50.8, -39.69) * mm});
            skLineSegment(sketch, "E37.0.6", {"start": v(50.8, -39.69) * mm, "end": v(50.8, -36.91) * mm});
            skLineSegment(sketch, "E38.0.0", {"start": v(47.62, 34.37) * mm, "end": v(50.8, 34.37) * mm});
            skLineSegment(sketch, "E38.0.1", {"start": v(50.8, 34.37) * mm, "end": v(50.8, 42.07) * mm});
            skLineSegment(sketch, "E38.0.2", {"start": v(50.8, 42.07) * mm, "end": v(47.62, 42.07) * mm});
            skLineSegment(sketch, "E38.0.3", {"start": v(47.62, 42.07) * mm, "end": v(47.62, 38.9) * mm});
            skLineSegment(sketch, "E38.0.4", {"start": v(47.62, 38.9) * mm, "end": v(47.62, 34.37) * mm});
            skSolve(sketch);
        }
        {
            var Q0;
            Q0=makeQuery(id+"F13.imprint","IMPRINT",FACE,{"disambiguationData":[TD([[makeQuery(id+"F13.imprint","IMPRINT",EDGE,{"derivedFrom":sQuery(id+"F13.wireOp",EDGE,"E38.0.0")}),1.0]])]});
            var Q1;
            Q1=makeQuery(id+"F13.imprint","IMPRINT",FACE,{"disambiguationData":[TD([[makeQuery(id+"F13.imprint","IMPRINT",EDGE,{"derivedFrom":sQuery(id+"F13.wireOp",EDGE,"E36.0.0")}),1.0]])]});
            var Q2;
            Q2=makeQuery(id+"F13.imprint","IMPRINT",FACE,{"disambiguationData":[TD([[makeQuery(id+"F13.imprint","IMPRINT",EDGE,{"derivedFrom":sQuery(id+"F13.wireOp",EDGE,"E37.0.0")}),-1.0]])]});
            extrude(context, id + "F14", {"entities" : qUnion([Q0, Q1, Q2]), "operationType" : NewBodyOperationType.ADD, "oppositeDirection" : true, "depth" : 3.97 * mm});
        }
    });
